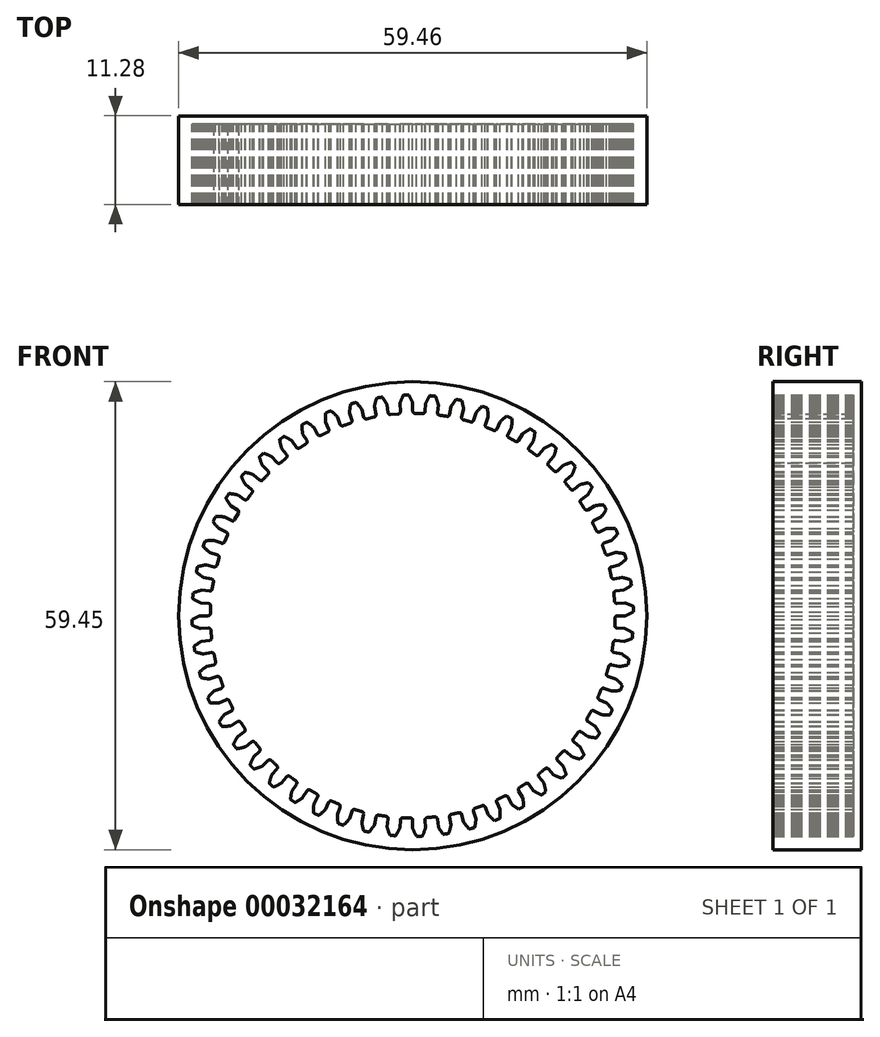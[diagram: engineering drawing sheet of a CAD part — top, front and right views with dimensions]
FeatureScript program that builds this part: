
annotation { "Feature Type Name" : "Feature", "Feature Type Description" : "" }
export const myFeature = defineFeature(function(context is Context, id is Id, definition is map)
    precondition{}
    {
        {
            var Q0;
            Q0=qCreatedBy(makeId("Front.planeOp"),FACE);
            var sketch = newSketch(context, id + "F0", { "sketchPlane" : qUnion([Q0])});
            skLineSegment(sketch, "E0", {"start": v(0, 25.05) * mm, "end": v(0, 26.31) * mm});
            skArc(sketch, "E1.trimOffspring", {"start": v(0, 26.31) * mm, "mid": v(-0.22, 26.83) * mm, "end": v(-0.48, 27.32) * mm});
            skArc(sketch, "E2.0.MirrorCS", {"start": v(-1.59, 26.26) * mm, "mid": v(-1.4, 26.8) * mm, "end": v(-1.17, 27.3) * mm});
            skLineSegment(sketch, "E3.0.MirrorCS", {"start": v(-1.51, 25) * mm, "end": v(-1.59, 26.26) * mm});
            skPoint(sketch, "E4.orphan", {"position": v(-2.02, 33.36) * mm});
            skArc(sketch, "E5.trimOffspring", {"start": v(-0.48, 27.32) * mm, "mid": v(-0.83, 27.31) * mm, "end": v(-1.17, 27.3) * mm});
            skLineSegment(sketch, "E6.1.0", {"start": v(-4.52, 24.64) * mm, "end": v(-4.75, 25.88) * mm});
            skLineSegment(sketch, "E6.1.1", {"start": v(-3.02, 24.86) * mm, "end": v(-3.18, 26.12) * mm});
            skArc(sketch, "E6.1.2", {"start": v(-4.75, 25.88) * mm, "mid": v(-4.62, 26.43) * mm, "end": v(-4.46, 26.96) * mm});
            skArc(sketch, "E6.1.3", {"start": v(-3.18, 26.12) * mm, "mid": v(-3.46, 26.6) * mm, "end": v(-3.77, 27.06) * mm});
            skArc(sketch, "E6.1.4", {"start": v(-3.77, 27.06) * mm, "mid": v(-4.12, 27.01) * mm, "end": v(-4.46, 26.96) * mm});
            skLineSegment(sketch, "E6.2.0", {"start": v(-7.46, 23.91) * mm, "end": v(-7.84, 25.12) * mm});
            skLineSegment(sketch, "E6.2.1", {"start": v(-6, 24.32) * mm, "end": v(-6.3, 25.55) * mm});
            skArc(sketch, "E6.2.2", {"start": v(-7.84, 25.12) * mm, "mid": v(-7.78, 25.68) * mm, "end": v(-7.68, 26.23) * mm});
            skArc(sketch, "E6.2.3", {"start": v(-6.3, 25.55) * mm, "mid": v(-6.64, 26) * mm, "end": v(-7.01, 26.41) * mm});
            skArc(sketch, "E6.2.4", {"start": v(-7.01, 26.41) * mm, "mid": v(-7.34, 26.32) * mm, "end": v(-7.68, 26.23) * mm});
            skLineSegment(sketch, "E6.3.0", {"start": v(-10.3, 22.84) * mm, "end": v(-10.8, 24) * mm});
            skLineSegment(sketch, "E6.3.1", {"start": v(-8.9, 23.42) * mm, "end": v(-9.34, 24.6) * mm});
            skArc(sketch, "E6.3.2", {"start": v(-10.8, 24) * mm, "mid": v(-10.82, 24.55) * mm, "end": v(-10.78, 25.1) * mm});
            skArc(sketch, "E6.3.3", {"start": v(-9.34, 24.6) * mm, "mid": v(-9.73, 25) * mm, "end": v(-10.15, 25.37) * mm});
            skArc(sketch, "E6.3.4", {"start": v(-10.15, 25.37) * mm, "mid": v(-10.47, 25.24) * mm, "end": v(-10.78, 25.1) * mm});
            skLineSegment(sketch, "E6.4.0", {"start": v(-12.97, 21.43) * mm, "end": v(-13.63, 22.51) * mm});
            skLineSegment(sketch, "E6.4.1", {"start": v(-11.65, 22.17) * mm, "end": v(-12.24, 23.3) * mm});
            skArc(sketch, "E6.4.2", {"start": v(-13.63, 22.51) * mm, "mid": v(-13.7, 23.07) * mm, "end": v(-13.74, 23.63) * mm});
            skArc(sketch, "E6.4.3", {"start": v(-12.24, 23.3) * mm, "mid": v(-12.67, 23.65) * mm, "end": v(-13.14, 23.96) * mm});
            skArc(sketch, "E6.4.4", {"start": v(-13.14, 23.96) * mm, "mid": v(-13.44, 23.8) * mm, "end": v(-13.74, 23.63) * mm});
            skLineSegment(sketch, "E6.5.0", {"start": v(-15.46, 19.71) * mm, "end": v(-16.24, 20.7) * mm});
            skLineSegment(sketch, "E6.5.1", {"start": v(-14.24, 20.6) * mm, "end": v(-14.96, 21.65) * mm});
            skArc(sketch, "E6.5.2", {"start": v(-16.24, 20.7) * mm, "mid": v(-16.39, 21.25) * mm, "end": v(-16.49, 21.8) * mm});
            skArc(sketch, "E6.5.3", {"start": v(-14.96, 21.65) * mm, "mid": v(-15.44, 21.95) * mm, "end": v(-15.93, 22.2) * mm});
            skArc(sketch, "E6.5.4", {"start": v(-15.93, 22.2) * mm, "mid": v(-16.21, 22) * mm, "end": v(-16.49, 21.8) * mm});
            skLineSegment(sketch, "E6.6.0", {"start": v(-17.73, 17.7) * mm, "end": v(-18.63, 18.6) * mm});
            skLineSegment(sketch, "E6.6.1", {"start": v(-16.63, 18.74) * mm, "end": v(-17.47, 19.69) * mm});
            skArc(sketch, "E6.6.2", {"start": v(-18.63, 18.6) * mm, "mid": v(-18.83, 19.12) * mm, "end": v(-19, 19.65) * mm});
            skArc(sketch, "E6.6.3", {"start": v(-17.47, 19.69) * mm, "mid": v(-17.97, 19.93) * mm, "end": v(-18.5, 20.12) * mm});
            skArc(sketch, "E6.6.4", {"start": v(-18.5, 20.12) * mm, "mid": v(-18.75, 19.89) * mm, "end": v(-19, 19.65) * mm});
            skLineSegment(sketch, "E6.7.0", {"start": v(-19.74, 15.44) * mm, "end": v(-20.73, 16.22) * mm});
            skLineSegment(sketch, "E6.7.1", {"start": v(-18.77, 16.6) * mm, "end": v(-19.72, 17.44) * mm});
            skArc(sketch, "E6.7.2", {"start": v(-20.73, 16.22) * mm, "mid": v(-21, 16.7) * mm, "end": v(-21.23, 17.22) * mm});
            skArc(sketch, "E6.7.3", {"start": v(-19.72, 17.44) * mm, "mid": v(-20.25, 17.62) * mm, "end": v(-20.8, 17.75) * mm});
            skArc(sketch, "E6.7.4", {"start": v(-20.8, 17.75) * mm, "mid": v(-21.01, 17.48) * mm, "end": v(-21.23, 17.22) * mm});
            skLineSegment(sketch, "E6.8.0", {"start": v(-21.46, 12.94) * mm, "end": v(-22.54, 13.6) * mm});
            skLineSegment(sketch, "E6.8.1", {"start": v(-20.64, 14.22) * mm, "end": v(-21.68, 14.93) * mm});
            skArc(sketch, "E6.8.2", {"start": v(-22.54, 13.6) * mm, "mid": v(-22.87, 14.05) * mm, "end": v(-23.16, 14.53) * mm});
            skArc(sketch, "E6.8.3", {"start": v(-21.68, 14.93) * mm, "mid": v(-22.23, 15.05) * mm, "end": v(-22.78, 15.11) * mm});
            skArc(sketch, "E6.8.4", {"start": v(-22.78, 15.11) * mm, "mid": v(-22.97, 14.82) * mm, "end": v(-23.16, 14.53) * mm});
            skLineSegment(sketch, "E6.9.0", {"start": v(-22.86, 10.26) * mm, "end": v(-24.02, 10.78) * mm});
            skLineSegment(sketch, "E6.9.1", {"start": v(-22.2, 11.62) * mm, "end": v(-23.32, 12.21) * mm});
            skArc(sketch, "E6.9.2", {"start": v(-24.02, 10.78) * mm, "mid": v(-24.4, 11.2) * mm, "end": v(-24.74, 11.64) * mm});
            skArc(sketch, "E6.9.3", {"start": v(-23.32, 12.21) * mm, "mid": v(-23.88, 12.26) * mm, "end": v(-24.44, 12.26) * mm});
            skArc(sketch, "E6.9.4", {"start": v(-24.44, 12.26) * mm, "mid": v(-24.6, 11.95) * mm, "end": v(-24.74, 11.64) * mm});
            skLineSegment(sketch, "E6.10.0", {"start": v(-23.94, 7.43) * mm, "end": v(-25.15, 7.8) * mm});
            skLineSegment(sketch, "E6.10.1", {"start": v(-23.44, 8.86) * mm, "end": v(-24.63, 9.31) * mm});
            skArc(sketch, "E6.10.2", {"start": v(-25.15, 7.8) * mm, "mid": v(-25.57, 8.17) * mm, "end": v(-25.97, 8.57) * mm});
            skArc(sketch, "E6.10.3", {"start": v(-24.63, 9.31) * mm, "mid": v(-25.19, 9.29) * mm, "end": v(-25.74, 9.22) * mm});
            skArc(sketch, "E6.10.4", {"start": v(-25.74, 9.22) * mm, "mid": v(-25.86, 8.9) * mm, "end": v(-25.97, 8.57) * mm});
            skLineSegment(sketch, "E6.11.0", {"start": v(-24.66, 4.5) * mm, "end": v(-25.9, 4.72) * mm});
            skLineSegment(sketch, "E6.11.1", {"start": v(-24.35, 5.97) * mm, "end": v(-25.58, 6.28) * mm});
            skArc(sketch, "E6.11.2", {"start": v(-25.9, 4.72) * mm, "mid": v(-26.38, 5.03) * mm, "end": v(-26.81, 5.38) * mm});
            skArc(sketch, "E6.11.3", {"start": v(-25.58, 6.28) * mm, "mid": v(-26.13, 6.18) * mm, "end": v(-26.67, 6.05) * mm});
            skArc(sketch, "E6.11.4", {"start": v(-26.67, 6.05) * mm, "mid": v(-26.74, 5.71) * mm, "end": v(-26.81, 5.38) * mm});
            skLineSegment(sketch, "E6.12.0", {"start": v(-25.03, 1.49) * mm, "end": v(-26.3, 1.56) * mm});
            skLineSegment(sketch, "E6.12.1", {"start": v(-24.9, 3) * mm, "end": v(-26.15, 3.15) * mm});
            skArc(sketch, "E6.12.2", {"start": v(-26.3, 1.56) * mm, "mid": v(-26.8, 1.81) * mm, "end": v(-27.27, 2.1) * mm});
            skArc(sketch, "E6.12.3", {"start": v(-26.15, 3.15) * mm, "mid": v(-26.69, 3) * mm, "end": v(-27.2, 2.8) * mm});
            skArc(sketch, "E6.12.4", {"start": v(-27.2, 2.8) * mm, "mid": v(-27.24, 2.45) * mm, "end": v(-27.27, 2.1) * mm});
            skLineSegment(sketch, "E6.13.0", {"start": v(-25.03, -1.54) * mm, "end": v(-26.3, -1.62) * mm});
            skLineSegment(sketch, "E6.13.1", {"start": v(-25.07, -0.03) * mm, "end": v(-26.34, -0.03) * mm});
            skArc(sketch, "E6.13.2", {"start": v(-26.3, -1.62) * mm, "mid": v(-26.82, -1.43) * mm, "end": v(-27.33, -1.2) * mm});
            skArc(sketch, "E6.13.3", {"start": v(-26.34, -0.03) * mm, "mid": v(-26.85, -0.25) * mm, "end": v(-27.35, -0.5) * mm});
            skArc(sketch, "E6.13.4", {"start": v(-27.35, -0.5) * mm, "mid": v(-27.34, -0.85) * mm, "end": v(-27.33, -1.2) * mm});
            skLineSegment(sketch, "E6.14.0", {"start": v(-24.66, -4.55) * mm, "end": v(-25.9, -4.78) * mm});
            skLineSegment(sketch, "E6.14.1", {"start": v(-24.9, -3.05) * mm, "end": v(-26.15, -3.2) * mm});
            skArc(sketch, "E6.14.2", {"start": v(-25.9, -4.78) * mm, "mid": v(-26.45, -4.65) * mm, "end": v(-26.99, -4.48) * mm});
            skArc(sketch, "E6.14.3", {"start": v(-26.15, -3.2) * mm, "mid": v(-26.63, -3.48) * mm, "end": v(-27.1, -3.8) * mm});
            skArc(sketch, "E6.14.4", {"start": v(-27.1, -3.8) * mm, "mid": v(-27.04, -4.14) * mm, "end": v(-26.99, -4.48) * mm});
            skLineSegment(sketch, "E6.15.0", {"start": v(-23.94, -7.49) * mm, "end": v(-25.15, -7.86) * mm});
            skLineSegment(sketch, "E6.15.1", {"start": v(-24.35, -6.03) * mm, "end": v(-25.58, -6.33) * mm});
            skArc(sketch, "E6.15.2", {"start": v(-25.15, -7.86) * mm, "mid": v(-25.7, -7.8) * mm, "end": v(-26.25, -7.7) * mm});
            skArc(sketch, "E6.15.3", {"start": v(-25.58, -6.33) * mm, "mid": v(-26.02, -6.67) * mm, "end": v(-26.44, -7.04) * mm});
            skArc(sketch, "E6.15.4", {"start": v(-26.44, -7.04) * mm, "mid": v(-26.35, -7.37) * mm, "end": v(-26.25, -7.7) * mm});
            skLineSegment(sketch, "E6.16.0", {"start": v(-22.87, -10.32) * mm, "end": v(-24.02, -10.84) * mm});
            skLineSegment(sketch, "E6.16.1", {"start": v(-23.44, -8.92) * mm, "end": v(-24.63, -9.37) * mm});
            skArc(sketch, "E6.16.2", {"start": v(-24.02, -10.84) * mm, "mid": v(-24.58, -10.85) * mm, "end": v(-25.14, -10.81) * mm});
            skArc(sketch, "E6.16.3", {"start": v(-24.63, -9.37) * mm, "mid": v(-25.03, -9.76) * mm, "end": v(-25.4, -10.18) * mm});
            skArc(sketch, "E6.16.4", {"start": v(-25.4, -10.18) * mm, "mid": v(-25.27, -10.5) * mm, "end": v(-25.14, -10.81) * mm});
            skLineSegment(sketch, "E6.17.0", {"start": v(-21.46, -13) * mm, "end": v(-22.54, -13.65) * mm});
            skLineSegment(sketch, "E6.17.1", {"start": v(-22.2, -11.68) * mm, "end": v(-23.32, -12.27) * mm});
            skArc(sketch, "E6.17.2", {"start": v(-22.54, -13.65) * mm, "mid": v(-23.1, -13.73) * mm, "end": v(-23.65, -13.76) * mm});
            skArc(sketch, "E6.17.3", {"start": v(-23.32, -12.27) * mm, "mid": v(-23.68, -12.7) * mm, "end": v(-24, -13.16) * mm});
            skArc(sketch, "E6.17.4", {"start": v(-24, -13.16) * mm, "mid": v(-23.83, -13.47) * mm, "end": v(-23.65, -13.76) * mm});
            skLineSegment(sketch, "E6.18.0", {"start": v(-19.74, -15.5) * mm, "end": v(-20.74, -16.27) * mm});
            skLineSegment(sketch, "E6.18.1", {"start": v(-20.64, -14.27) * mm, "end": v(-21.68, -15) * mm});
            skArc(sketch, "E6.18.2", {"start": v(-20.74, -16.27) * mm, "mid": v(-21.28, -16.42) * mm, "end": v(-21.83, -16.52) * mm});
            skArc(sketch, "E6.18.3", {"start": v(-21.68, -15) * mm, "mid": v(-21.98, -15.46) * mm, "end": v(-22.23, -15.96) * mm});
            skArc(sketch, "E6.18.4", {"start": v(-22.23, -15.96) * mm, "mid": v(-22.03, -16.24) * mm, "end": v(-21.83, -16.52) * mm});
            skLineSegment(sketch, "E6.19.0", {"start": v(-17.73, -17.76) * mm, "end": v(-18.63, -18.65) * mm});
            skLineSegment(sketch, "E6.19.1", {"start": v(-18.77, -16.66) * mm, "end": v(-19.72, -17.5) * mm});
            skArc(sketch, "E6.19.2", {"start": v(-18.63, -18.65) * mm, "mid": v(-19.15, -18.86) * mm, "end": v(-19.68, -19.03) * mm});
            skArc(sketch, "E6.19.3", {"start": v(-19.72, -17.5) * mm, "mid": v(-19.96, -18) * mm, "end": v(-20.15, -18.52) * mm});
            skArc(sketch, "E6.19.4", {"start": v(-20.15, -18.52) * mm, "mid": v(-19.92, -18.78) * mm, "end": v(-19.68, -19.03) * mm});
            skLineSegment(sketch, "E6.20.0", {"start": v(-15.46, -19.77) * mm, "end": v(-16.25, -20.76) * mm});
            skLineSegment(sketch, "E6.20.1", {"start": v(-16.63, -18.8) * mm, "end": v(-17.47, -19.74) * mm});
            skArc(sketch, "E6.20.2", {"start": v(-16.25, -20.76) * mm, "mid": v(-16.74, -21.03) * mm, "end": v(-17.25, -21.26) * mm});
            skArc(sketch, "E6.20.3", {"start": v(-17.47, -19.74) * mm, "mid": v(-17.64, -20.28) * mm, "end": v(-17.78, -20.82) * mm});
            skArc(sketch, "E6.20.4", {"start": v(-17.78, -20.82) * mm, "mid": v(-17.51, -21.04) * mm, "end": v(-17.25, -21.26) * mm});
            skLineSegment(sketch, "E6.21.0", {"start": v(-12.97, -21.49) * mm, "end": v(-13.63, -22.57) * mm});
            skLineSegment(sketch, "E6.21.1", {"start": v(-14.24, -20.66) * mm, "end": v(-14.96, -21.7) * mm});
            skArc(sketch, "E6.21.2", {"start": v(-13.63, -22.57) * mm, "mid": v(-14.08, -22.9) * mm, "end": v(-14.56, -23.18) * mm});
            skArc(sketch, "E6.21.3", {"start": v(-14.96, -21.7) * mm, "mid": v(-15.07, -22.25) * mm, "end": v(-15.14, -22.8) * mm});
            skArc(sketch, "E6.21.4", {"start": v(-15.14, -22.8) * mm, "mid": v(-14.85, -23) * mm, "end": v(-14.56, -23.18) * mm});
            skLineSegment(sketch, "E6.22.0", {"start": v(-10.3, -22.9) * mm, "end": v(-10.81, -24.05) * mm});
            skLineSegment(sketch, "E6.22.1", {"start": v(-11.65, -22.23) * mm, "end": v(-12.24, -23.35) * mm});
            skArc(sketch, "E6.22.2", {"start": v(-10.81, -24.05) * mm, "mid": v(-11.22, -24.43) * mm, "end": v(-11.66, -24.77) * mm});
            skArc(sketch, "E6.22.3", {"start": v(-12.24, -23.35) * mm, "mid": v(-12.29, -23.9) * mm, "end": v(-12.28, -24.47) * mm});
            skArc(sketch, "E6.22.4", {"start": v(-12.28, -24.47) * mm, "mid": v(-11.97, -24.62) * mm, "end": v(-11.66, -24.77) * mm});
            skLineSegment(sketch, "E6.23.0", {"start": v(-7.46, -23.97) * mm, "end": v(-7.84, -25.18) * mm});
            skLineSegment(sketch, "E6.23.1", {"start": v(-8.9, -23.47) * mm, "end": v(-9.34, -24.66) * mm});
            skArc(sketch, "E6.23.2", {"start": v(-7.84, -25.18) * mm, "mid": v(-8.2, -25.6) * mm, "end": v(-8.6, -26) * mm});
            skArc(sketch, "E6.23.3", {"start": v(-9.34, -24.66) * mm, "mid": v(-9.32, -25.22) * mm, "end": v(-9.25, -25.77) * mm});
            skArc(sketch, "E6.23.4", {"start": v(-9.25, -25.77) * mm, "mid": v(-8.92, -25.89) * mm, "end": v(-8.6, -26) * mm});
            skLineSegment(sketch, "E6.24.0", {"start": v(-4.52, -24.7) * mm, "end": v(-4.75, -25.94) * mm});
            skLineSegment(sketch, "E6.24.1", {"start": v(-6, -24.37) * mm, "end": v(-6.3, -25.6) * mm});
            skArc(sketch, "E6.24.2", {"start": v(-4.75, -25.94) * mm, "mid": v(-5.06, -26.4) * mm, "end": v(-5.4, -26.84) * mm});
            skArc(sketch, "E6.24.3", {"start": v(-6.3, -25.6) * mm, "mid": v(-6.21, -26.16) * mm, "end": v(-6.08, -26.7) * mm});
            skArc(sketch, "E6.24.4", {"start": v(-6.08, -26.7) * mm, "mid": v(-5.74, -26.77) * mm, "end": v(-5.4, -26.84) * mm});
            skLineSegment(sketch, "E6.25.0", {"start": v(-1.51, -25.06) * mm, "end": v(-1.6, -26.32) * mm});
            skLineSegment(sketch, "E6.25.1", {"start": v(-3.02, -24.92) * mm, "end": v(-3.18, -26.18) * mm});
            skArc(sketch, "E6.25.2", {"start": v(-1.6, -26.32) * mm, "mid": v(-1.84, -26.82) * mm, "end": v(-2.13, -27.3) * mm});
            skArc(sketch, "E6.25.3", {"start": v(-3.18, -26.18) * mm, "mid": v(-3.02, -26.71) * mm, "end": v(-2.82, -27.24) * mm});
            skArc(sketch, "E6.25.4", {"start": v(-2.82, -27.24) * mm, "mid": v(-2.48, -27.27) * mm, "end": v(-2.13, -27.3) * mm});
            skLineSegment(sketch, "E6.26.0", {"start": v(1.51, -25.06) * mm, "end": v(1.59, -26.32) * mm});
            skLineSegment(sketch, "E6.26.1", {"start": v(0, -25.1) * mm, "end": v(0, -26.37) * mm});
            skArc(sketch, "E6.26.2", {"start": v(1.59, -26.32) * mm, "mid": v(1.4, -26.85) * mm, "end": v(1.17, -27.36) * mm});
            skArc(sketch, "E6.26.3", {"start": v(0, -26.37) * mm, "mid": v(0.22, -26.88) * mm, "end": v(0.48, -27.38) * mm});
            skArc(sketch, "E6.26.4", {"start": v(0.48, -27.38) * mm, "mid": v(0.83, -27.37) * mm, "end": v(1.17, -27.36) * mm});
            skLineSegment(sketch, "E6.27.0", {"start": v(4.52, -24.7) * mm, "end": v(4.75, -25.94) * mm});
            skLineSegment(sketch, "E6.27.1", {"start": v(3.02, -24.92) * mm, "end": v(3.18, -26.18) * mm});
            skArc(sketch, "E6.27.2", {"start": v(4.75, -25.94) * mm, "mid": v(4.62, -26.48) * mm, "end": v(4.46, -27.02) * mm});
            skArc(sketch, "E6.27.3", {"start": v(3.18, -26.18) * mm, "mid": v(3.46, -26.66) * mm, "end": v(3.77, -27.12) * mm});
            skArc(sketch, "E6.27.4", {"start": v(3.77, -27.12) * mm, "mid": v(4.12, -27.07) * mm, "end": v(4.46, -27.02) * mm});
            skLineSegment(sketch, "E6.28.0", {"start": v(7.46, -23.97) * mm, "end": v(7.84, -25.18) * mm});
            skLineSegment(sketch, "E6.28.1", {"start": v(6, -24.37) * mm, "end": v(6.3, -25.6) * mm});
            skArc(sketch, "E6.28.2", {"start": v(7.84, -25.18) * mm, "mid": v(7.78, -25.73) * mm, "end": v(7.68, -26.28) * mm});
            skArc(sketch, "E6.28.3", {"start": v(6.3, -25.6) * mm, "mid": v(6.64, -26.05) * mm, "end": v(7.01, -26.47) * mm});
            skArc(sketch, "E6.28.4", {"start": v(7.01, -26.47) * mm, "mid": v(7.34, -26.38) * mm, "end": v(7.68, -26.28) * mm});
            skLineSegment(sketch, "E6.29.0", {"start": v(10.3, -22.9) * mm, "end": v(10.8, -24.05) * mm});
            skLineSegment(sketch, "E6.29.1", {"start": v(8.9, -23.47) * mm, "end": v(9.34, -24.66) * mm});
            skArc(sketch, "E6.29.2", {"start": v(10.8, -24.05) * mm, "mid": v(10.82, -24.6) * mm, "end": v(10.78, -25.17) * mm});
            skArc(sketch, "E6.29.3", {"start": v(9.34, -24.66) * mm, "mid": v(9.73, -25.06) * mm, "end": v(10.15, -25.43) * mm});
            skArc(sketch, "E6.29.4", {"start": v(10.15, -25.43) * mm, "mid": v(10.47, -25.3) * mm, "end": v(10.78, -25.17) * mm});
            skLineSegment(sketch, "E6.30.0", {"start": v(12.97, -21.49) * mm, "end": v(13.63, -22.57) * mm});
            skLineSegment(sketch, "E6.30.1", {"start": v(11.65, -22.23) * mm, "end": v(12.24, -23.35) * mm});
            skArc(sketch, "E6.30.2", {"start": v(13.63, -22.57) * mm, "mid": v(13.7, -23.12) * mm, "end": v(13.74, -23.68) * mm});
            skArc(sketch, "E6.30.3", {"start": v(12.24, -23.35) * mm, "mid": v(12.67, -23.7) * mm, "end": v(13.14, -24.02) * mm});
            skArc(sketch, "E6.30.4", {"start": v(13.14, -24.02) * mm, "mid": v(13.44, -23.85) * mm, "end": v(13.74, -23.68) * mm});
            skLineSegment(sketch, "E6.31.0", {"start": v(15.46, -19.77) * mm, "end": v(16.24, -20.76) * mm});
            skLineSegment(sketch, "E6.31.1", {"start": v(14.24, -20.66) * mm, "end": v(14.96, -21.7) * mm});
            skArc(sketch, "E6.31.2", {"start": v(16.24, -20.76) * mm, "mid": v(16.39, -21.3) * mm, "end": v(16.49, -21.85) * mm});
            skArc(sketch, "E6.31.3", {"start": v(14.96, -21.7) * mm, "mid": v(15.44, -22) * mm, "end": v(15.93, -22.26) * mm});
            skArc(sketch, "E6.31.4", {"start": v(15.93, -22.26) * mm, "mid": v(16.21, -22.06) * mm, "end": v(16.49, -21.85) * mm});
            skLineSegment(sketch, "E6.32.0", {"start": v(17.73, -17.76) * mm, "end": v(18.63, -18.65) * mm});
            skLineSegment(sketch, "E6.32.1", {"start": v(16.63, -18.8) * mm, "end": v(17.47, -19.74) * mm});
            skArc(sketch, "E6.32.2", {"start": v(18.63, -18.65) * mm, "mid": v(18.83, -19.17) * mm, "end": v(19, -19.7) * mm});
            skArc(sketch, "E6.32.3", {"start": v(17.47, -19.74) * mm, "mid": v(17.97, -19.98) * mm, "end": v(18.5, -20.18) * mm});
            skArc(sketch, "E6.32.4", {"start": v(18.5, -20.18) * mm, "mid": v(18.75, -19.95) * mm, "end": v(19, -19.7) * mm});
            skLineSegment(sketch, "E6.33.0", {"start": v(19.74, -15.5) * mm, "end": v(20.73, -16.27) * mm});
            skLineSegment(sketch, "E6.33.1", {"start": v(18.77, -16.66) * mm, "end": v(19.72, -17.5) * mm});
            skArc(sketch, "E6.33.2", {"start": v(20.73, -16.27) * mm, "mid": v(21, -16.76) * mm, "end": v(21.23, -17.27) * mm});
            skArc(sketch, "E6.33.3", {"start": v(19.72, -17.5) * mm, "mid": v(20.25, -17.67) * mm, "end": v(20.8, -17.8) * mm});
            skArc(sketch, "E6.33.4", {"start": v(20.8, -17.8) * mm, "mid": v(21.01, -17.54) * mm, "end": v(21.23, -17.27) * mm});
            skLineSegment(sketch, "E6.34.0", {"start": v(21.46, -13) * mm, "end": v(22.54, -13.66) * mm});
            skLineSegment(sketch, "E6.34.1", {"start": v(20.64, -14.27) * mm, "end": v(21.68, -15) * mm});
            skArc(sketch, "E6.34.2", {"start": v(22.54, -13.66) * mm, "mid": v(22.87, -14.11) * mm, "end": v(23.16, -14.59) * mm});
            skArc(sketch, "E6.34.3", {"start": v(21.68, -15) * mm, "mid": v(22.23, -15.1) * mm, "end": v(22.78, -15.17) * mm});
            skArc(sketch, "E6.34.4", {"start": v(22.78, -15.17) * mm, "mid": v(22.97, -14.88) * mm, "end": v(23.16, -14.59) * mm});
            skLineSegment(sketch, "E6.35.0", {"start": v(22.86, -10.32) * mm, "end": v(24.02, -10.84) * mm});
            skLineSegment(sketch, "E6.35.1", {"start": v(22.2, -11.68) * mm, "end": v(23.32, -12.27) * mm});
            skArc(sketch, "E6.35.2", {"start": v(24.02, -10.84) * mm, "mid": v(24.4, -11.25) * mm, "end": v(24.74, -11.7) * mm});
            skArc(sketch, "E6.35.3", {"start": v(23.32, -12.27) * mm, "mid": v(23.88, -12.31) * mm, "end": v(24.44, -12.31) * mm});
            skArc(sketch, "E6.35.4", {"start": v(24.44, -12.31) * mm, "mid": v(24.6, -12) * mm, "end": v(24.74, -11.7) * mm});
            skLineSegment(sketch, "E6.36.0", {"start": v(23.94, -7.49) * mm, "end": v(25.15, -7.87) * mm});
            skLineSegment(sketch, "E6.36.1", {"start": v(23.44, -8.92) * mm, "end": v(24.63, -9.37) * mm});
            skArc(sketch, "E6.36.2", {"start": v(25.15, -7.87) * mm, "mid": v(25.57, -8.23) * mm, "end": v(25.97, -8.63) * mm});
            skArc(sketch, "E6.36.3", {"start": v(24.63, -9.37) * mm, "mid": v(25.19, -9.35) * mm, "end": v(25.74, -9.28) * mm});
            skArc(sketch, "E6.36.4", {"start": v(25.74, -9.28) * mm, "mid": v(25.86, -8.95) * mm, "end": v(25.97, -8.63) * mm});
            skLineSegment(sketch, "E6.37.0", {"start": v(24.66, -4.55) * mm, "end": v(25.9, -4.78) * mm});
            skLineSegment(sketch, "E6.37.1", {"start": v(24.35, -6.03) * mm, "end": v(25.58, -6.33) * mm});
            skArc(sketch, "E6.37.2", {"start": v(25.9, -4.78) * mm, "mid": v(26.38, -5.09) * mm, "end": v(26.81, -5.43) * mm});
            skArc(sketch, "E6.37.3", {"start": v(25.58, -6.33) * mm, "mid": v(26.13, -6.24) * mm, "end": v(26.67, -6.1) * mm});
            skArc(sketch, "E6.37.4", {"start": v(26.67, -6.1) * mm, "mid": v(26.74, -5.77) * mm, "end": v(26.81, -5.43) * mm});
            skLineSegment(sketch, "E6.38.0", {"start": v(25.03, -1.54) * mm, "end": v(26.3, -1.62) * mm});
            skLineSegment(sketch, "E6.38.1", {"start": v(24.9, -3.05) * mm, "end": v(26.15, -3.2) * mm});
            skArc(sketch, "E6.38.2", {"start": v(26.3, -1.62) * mm, "mid": v(26.8, -1.87) * mm, "end": v(27.27, -2.16) * mm});
            skArc(sketch, "E6.38.3", {"start": v(26.15, -3.2) * mm, "mid": v(26.69, -3.05) * mm, "end": v(27.2, -2.85) * mm});
            skArc(sketch, "E6.38.4", {"start": v(27.2, -2.85) * mm, "mid": v(27.24, -2.5) * mm, "end": v(27.27, -2.16) * mm});
            skLineSegment(sketch, "E6.39.0", {"start": v(25.03, 1.48) * mm, "end": v(26.3, 1.56) * mm});
            skLineSegment(sketch, "E6.39.1", {"start": v(25.07, -0.03) * mm, "end": v(26.34, -0.03) * mm});
            skArc(sketch, "E6.39.2", {"start": v(26.3, 1.56) * mm, "mid": v(26.82, 1.37) * mm, "end": v(27.33, 1.14) * mm});
            skArc(sketch, "E6.39.3", {"start": v(26.34, -0.03) * mm, "mid": v(26.85, 0.2) * mm, "end": v(27.35, 0.45) * mm});
            skArc(sketch, "E6.39.4", {"start": v(27.35, 0.45) * mm, "mid": v(27.34, 0.8) * mm, "end": v(27.33, 1.14) * mm});
            skLineSegment(sketch, "E6.40.0", {"start": v(24.66, 4.5) * mm, "end": v(25.9, 4.72) * mm});
            skLineSegment(sketch, "E6.40.1", {"start": v(24.9, 3) * mm, "end": v(26.15, 3.15) * mm});
            skArc(sketch, "E6.40.2", {"start": v(25.9, 4.72) * mm, "mid": v(26.45, 4.6) * mm, "end": v(26.99, 4.43) * mm});
            skArc(sketch, "E6.40.3", {"start": v(26.15, 3.15) * mm, "mid": v(26.63, 3.43) * mm, "end": v(27.1, 3.75) * mm});
            skArc(sketch, "E6.40.4", {"start": v(27.1, 3.75) * mm, "mid": v(27.04, 4.09) * mm, "end": v(26.99, 4.43) * mm});
            skLineSegment(sketch, "E6.41.0", {"start": v(23.94, 7.43) * mm, "end": v(25.15, 7.8) * mm});
            skLineSegment(sketch, "E6.41.1", {"start": v(24.35, 5.97) * mm, "end": v(25.58, 6.28) * mm});
            skArc(sketch, "E6.41.2", {"start": v(25.15, 7.8) * mm, "mid": v(25.7, 7.75) * mm, "end": v(26.25, 7.65) * mm});
            skArc(sketch, "E6.41.3", {"start": v(25.58, 6.28) * mm, "mid": v(26.02, 6.61) * mm, "end": v(26.44, 6.98) * mm});
            skArc(sketch, "E6.41.4", {"start": v(26.44, 6.98) * mm, "mid": v(26.35, 7.32) * mm, "end": v(26.25, 7.65) * mm});
            skLineSegment(sketch, "E6.42.0", {"start": v(22.87, 10.26) * mm, "end": v(24.02, 10.78) * mm});
            skLineSegment(sketch, "E6.42.1", {"start": v(23.44, 8.86) * mm, "end": v(24.63, 9.31) * mm});
            skArc(sketch, "E6.42.2", {"start": v(24.02, 10.78) * mm, "mid": v(24.58, 10.8) * mm, "end": v(25.14, 10.76) * mm});
            skArc(sketch, "E6.42.3", {"start": v(24.63, 9.31) * mm, "mid": v(25.03, 9.7) * mm, "end": v(25.4, 10.12) * mm});
            skArc(sketch, "E6.42.4", {"start": v(25.4, 10.12) * mm, "mid": v(25.27, 10.44) * mm, "end": v(25.14, 10.76) * mm});
            skLineSegment(sketch, "E6.43.0", {"start": v(21.46, 12.94) * mm, "end": v(22.54, 13.6) * mm});
            skLineSegment(sketch, "E6.43.1", {"start": v(22.2, 11.62) * mm, "end": v(23.32, 12.21) * mm});
            skArc(sketch, "E6.43.2", {"start": v(22.54, 13.6) * mm, "mid": v(23.1, 13.68) * mm, "end": v(23.65, 13.7) * mm});
            skArc(sketch, "E6.43.3", {"start": v(23.32, 12.21) * mm, "mid": v(23.68, 12.65) * mm, "end": v(24, 13.1) * mm});
            skArc(sketch, "E6.43.4", {"start": v(24, 13.1) * mm, "mid": v(23.83, 13.4) * mm, "end": v(23.65, 13.7) * mm});
            skLineSegment(sketch, "E6.44.0", {"start": v(19.74, 15.43) * mm, "end": v(20.74, 16.22) * mm});
            skLineSegment(sketch, "E6.44.1", {"start": v(20.64, 14.22) * mm, "end": v(21.68, 14.93) * mm});
            skArc(sketch, "E6.44.2", {"start": v(20.74, 16.22) * mm, "mid": v(21.28, 16.36) * mm, "end": v(21.83, 16.46) * mm});
            skArc(sketch, "E6.44.3", {"start": v(21.68, 14.93) * mm, "mid": v(21.98, 15.4) * mm, "end": v(22.23, 15.9) * mm});
            skArc(sketch, "E6.44.4", {"start": v(22.23, 15.9) * mm, "mid": v(22.03, 16.18) * mm, "end": v(21.83, 16.46) * mm});
            skLineSegment(sketch, "E6.45.0", {"start": v(17.73, 17.7) * mm, "end": v(18.63, 18.6) * mm});
            skLineSegment(sketch, "E6.45.1", {"start": v(18.77, 16.6) * mm, "end": v(19.72, 17.44) * mm});
            skArc(sketch, "E6.45.2", {"start": v(18.63, 18.6) * mm, "mid": v(19.15, 18.8) * mm, "end": v(19.68, 18.97) * mm});
            skArc(sketch, "E6.45.3", {"start": v(19.72, 17.44) * mm, "mid": v(19.96, 17.94) * mm, "end": v(20.15, 18.47) * mm});
            skArc(sketch, "E6.45.4", {"start": v(20.15, 18.47) * mm, "mid": v(19.92, 18.72) * mm, "end": v(19.68, 18.97) * mm});
            skLineSegment(sketch, "E6.46.0", {"start": v(15.46, 19.7) * mm, "end": v(16.25, 20.7) * mm});
            skLineSegment(sketch, "E6.46.1", {"start": v(16.63, 18.74) * mm, "end": v(17.47, 19.69) * mm});
            skArc(sketch, "E6.46.2", {"start": v(16.25, 20.7) * mm, "mid": v(16.74, 20.98) * mm, "end": v(17.25, 21.2) * mm});
            skArc(sketch, "E6.46.3", {"start": v(17.47, 19.69) * mm, "mid": v(17.64, 20.22) * mm, "end": v(17.78, 20.76) * mm});
            skArc(sketch, "E6.46.4", {"start": v(17.78, 20.76) * mm, "mid": v(17.51, 20.98) * mm, "end": v(17.25, 21.2) * mm});
            skLineSegment(sketch, "E6.47.0", {"start": v(12.97, 21.43) * mm, "end": v(13.63, 22.51) * mm});
            skLineSegment(sketch, "E6.47.1", {"start": v(14.24, 20.6) * mm, "end": v(14.96, 21.65) * mm});
            skArc(sketch, "E6.47.2", {"start": v(13.63, 22.51) * mm, "mid": v(14.08, 22.84) * mm, "end": v(14.56, 23.13) * mm});
            skArc(sketch, "E6.47.3", {"start": v(14.96, 21.65) * mm, "mid": v(15.07, 22.2) * mm, "end": v(15.14, 22.75) * mm});
            skArc(sketch, "E6.47.4", {"start": v(15.14, 22.75) * mm, "mid": v(14.85, 22.94) * mm, "end": v(14.56, 23.13) * mm});
            skLineSegment(sketch, "E6.48.0", {"start": v(10.3, 22.84) * mm, "end": v(10.81, 24) * mm});
            skLineSegment(sketch, "E6.48.1", {"start": v(11.65, 22.17) * mm, "end": v(12.24, 23.3) * mm});
            skArc(sketch, "E6.48.2", {"start": v(10.81, 24) * mm, "mid": v(11.22, 24.37) * mm, "end": v(11.66, 24.71) * mm});
            skArc(sketch, "E6.48.3", {"start": v(12.24, 23.3) * mm, "mid": v(12.29, 23.85) * mm, "end": v(12.28, 24.41) * mm});
            skArc(sketch, "E6.48.4", {"start": v(12.28, 24.41) * mm, "mid": v(11.97, 24.56) * mm, "end": v(11.66, 24.71) * mm});
            skLineSegment(sketch, "E6.49.0", {"start": v(7.46, 23.91) * mm, "end": v(7.84, 25.12) * mm});
            skLineSegment(sketch, "E6.49.1", {"start": v(8.9, 23.42) * mm, "end": v(9.34, 24.6) * mm});
            skArc(sketch, "E6.49.2", {"start": v(7.84, 25.12) * mm, "mid": v(8.2, 25.54) * mm, "end": v(8.6, 25.94) * mm});
            skArc(sketch, "E6.49.3", {"start": v(9.34, 24.6) * mm, "mid": v(9.32, 25.16) * mm, "end": v(9.25, 25.71) * mm});
            skArc(sketch, "E6.49.4", {"start": v(9.25, 25.71) * mm, "mid": v(8.92, 25.83) * mm, "end": v(8.6, 25.94) * mm});
            skLineSegment(sketch, "E6.50.0", {"start": v(4.52, 24.64) * mm, "end": v(4.75, 25.88) * mm});
            skLineSegment(sketch, "E6.50.1", {"start": v(6, 24.32) * mm, "end": v(6.3, 25.55) * mm});
            skArc(sketch, "E6.50.2", {"start": v(4.75, 25.88) * mm, "mid": v(5.06, 26.35) * mm, "end": v(5.4, 26.79) * mm});
            skArc(sketch, "E6.50.3", {"start": v(6.3, 25.55) * mm, "mid": v(6.21, 26.1) * mm, "end": v(6.08, 26.64) * mm});
            skArc(sketch, "E6.50.4", {"start": v(6.08, 26.64) * mm, "mid": v(5.74, 26.72) * mm, "end": v(5.4, 26.79) * mm});
            skLineSegment(sketch, "E6.51.0", {"start": v(1.51, 25) * mm, "end": v(1.6, 26.26) * mm});
            skLineSegment(sketch, "E6.51.1", {"start": v(3.02, 24.86) * mm, "end": v(3.18, 26.12) * mm});
            skArc(sketch, "E6.51.2", {"start": v(1.6, 26.26) * mm, "mid": v(1.84, 26.76) * mm, "end": v(2.13, 27.24) * mm});
            skArc(sketch, "E6.51.3", {"start": v(3.18, 26.12) * mm, "mid": v(3.02, 26.66) * mm, "end": v(2.82, 27.18) * mm});
            skArc(sketch, "E6.51.4", {"start": v(2.82, 27.18) * mm, "mid": v(2.48, 27.21) * mm, "end": v(2.13, 27.24) * mm});
            skCircle(sketch, "E7", {"center": v(0, -0.03) * mm, "radius": 29 * mm});
            skArc(sketch, "E8.trimOffspring", {"start": v(1.51, 25) * mm, "mid": v(0.76, 25.03) * mm, "end": v(0, 25.05) * mm});
            skArc(sketch, "E9.trimOffspring", {"start": v(4.52, 24.64) * mm, "mid": v(3.77, 24.76) * mm, "end": v(3.02, 24.86) * mm});
            skArc(sketch, "E10.trimOffspring", {"start": v(7.46, 23.91) * mm, "mid": v(6.73, 24.12) * mm, "end": v(6, 24.32) * mm});
            skArc(sketch, "E11.trimOffspring", {"start": v(10.3, 22.84) * mm, "mid": v(9.6, 23.14) * mm, "end": v(8.9, 23.42) * mm});
            skArc(sketch, "E12.trimOffspring", {"start": v(12.97, 21.43) * mm, "mid": v(12.32, 21.81) * mm, "end": v(11.65, 22.17) * mm});
            skArc(sketch, "E13.trimOffspring", {"start": v(15.46, 19.7) * mm, "mid": v(14.86, 20.17) * mm, "end": v(14.24, 20.6) * mm});
            skArc(sketch, "E14.trimOffspring", {"start": v(17.73, 17.7) * mm, "mid": v(17.19, 18.23) * mm, "end": v(16.63, 18.74) * mm});
            skArc(sketch, "E15.trimOffspring", {"start": v(19.74, 15.43) * mm, "mid": v(19.26, 16.02) * mm, "end": v(18.77, 16.6) * mm});
            skArc(sketch, "E16.trimOffspring", {"start": v(21.46, 12.94) * mm, "mid": v(21.06, 13.59) * mm, "end": v(20.64, 14.22) * mm});
            skArc(sketch, "E17.trimOffspring", {"start": v(22.87, 10.26) * mm, "mid": v(22.54, 10.95) * mm, "end": v(22.2, 11.62) * mm});
            skArc(sketch, "E18.trimOffspring", {"start": v(23.94, 7.43) * mm, "mid": v(23.7, 8.15) * mm, "end": v(23.44, 8.86) * mm});
            skArc(sketch, "E19.trimOffspring", {"start": v(-7.46, 23.91) * mm, "mid": v(-8.18, 23.67) * mm, "end": v(-8.9, 23.42) * mm});
            skArc(sketch, "E20.trimOffspring", {"start": v(-12.97, 21.43) * mm, "mid": v(-13.61, 21.03) * mm, "end": v(-14.24, 20.6) * mm});
            skLineSegment(sketch, "E21", {"start": v(-6, 24.32) * mm, "end": v(-4.52, 24.64) * mm});
            skLineSegment(sketch, "E22", {"start": v(-3.02, 24.86) * mm, "end": v(-1.51, 25) * mm});
            skArc(sketch, "E23.trimOffspring", {"start": v(-10.3, 22.84) * mm, "mid": v(-10.98, 22.52) * mm, "end": v(-11.65, 22.17) * mm});
            skArc(sketch, "E24.trimOffspring", {"start": v(-17.73, 17.7) * mm, "mid": v(-18.26, 17.16) * mm, "end": v(-18.77, 16.6) * mm});
            skArc(sketch, "E25.trimOffspring", {"start": v(-19.74, 15.44) * mm, "mid": v(-20.2, 14.83) * mm, "end": v(-20.64, 14.22) * mm});
            skArc(sketch, "E26.trimOffspring", {"start": v(-25.03, 1.49) * mm, "mid": v(-25.06, 0.73) * mm, "end": v(-25.07, -0.03) * mm});
            skArc(sketch, "E27.trimOffspring", {"start": v(-25.03, -1.54) * mm, "mid": v(-24.97, -2.3) * mm, "end": v(-24.9, -3.05) * mm});
            skArc(sketch, "E28.trimOffspring", {"start": v(-24.66, -4.55) * mm, "mid": v(-24.52, -5.3) * mm, "end": v(-24.35, -6.03) * mm});
            skArc(sketch, "E29.trimOffspring", {"start": v(-23.94, -7.49) * mm, "mid": v(-23.7, -8.2) * mm, "end": v(-23.44, -8.92) * mm});
            skArc(sketch, "E30.trimOffspring", {"start": v(24.66, 4.5) * mm, "mid": v(24.52, 5.23) * mm, "end": v(24.35, 5.97) * mm});
            skArc(sketch, "E31.trimOffspring", {"start": v(25.03, 1.48) * mm, "mid": v(24.97, 2.24) * mm, "end": v(24.9, 3) * mm});
            skArc(sketch, "E32.trimOffspring", {"start": v(25.03, -1.54) * mm, "mid": v(25.06, -0.79) * mm, "end": v(25.07, -0.03) * mm});
            skArc(sketch, "E33.trimOffspring", {"start": v(24.66, -4.55) * mm, "mid": v(24.79, -3.8) * mm, "end": v(24.9, -3.05) * mm});
            skArc(sketch, "E34.trimOffspring", {"start": v(23.94, -7.49) * mm, "mid": v(24.15, -6.76) * mm, "end": v(24.35, -6.03) * mm});
            skArc(sketch, "E35.trimOffspring", {"start": v(22.86, -10.32) * mm, "mid": v(23.17, -9.62) * mm, "end": v(23.44, -8.92) * mm});
            skArc(sketch, "E36.trimOffspring", {"start": v(21.46, -13) * mm, "mid": v(21.84, -12.35) * mm, "end": v(22.2, -11.68) * mm});
            skArc(sketch, "E37.trimOffspring", {"start": v(19.74, -15.5) * mm, "mid": v(20.2, -14.89) * mm, "end": v(20.64, -14.27) * mm});
            skArc(sketch, "E38.trimOffspring", {"start": v(17.73, -17.76) * mm, "mid": v(18.26, -17.22) * mm, "end": v(18.77, -16.66) * mm});
            skArc(sketch, "E39.trimOffspring", {"start": v(15.46, -19.77) * mm, "mid": v(16.05, -19.3) * mm, "end": v(16.63, -18.8) * mm});
            skArc(sketch, "E40.trimOffspring", {"start": v(12.97, -21.49) * mm, "mid": v(13.61, -21.09) * mm, "end": v(14.24, -20.66) * mm});
            skArc(sketch, "E41.trimOffspring", {"start": v(10.3, -22.9) * mm, "mid": v(10.98, -22.57) * mm, "end": v(11.65, -22.23) * mm});
            skArc(sketch, "E42.trimOffspring", {"start": v(7.46, -23.97) * mm, "mid": v(8.18, -23.73) * mm, "end": v(8.9, -23.47) * mm});
            skArc(sketch, "E43.trimOffspring", {"start": v(4.52, -24.7) * mm, "mid": v(5.26, -24.54) * mm, "end": v(6, -24.37) * mm});
            skArc(sketch, "E44.trimOffspring", {"start": v(1.51, -25.06) * mm, "mid": v(2.27, -25) * mm, "end": v(3.02, -24.92) * mm});
            skArc(sketch, "E45.trimOffspring", {"start": v(-1.51, -25.06) * mm, "mid": v(-0.76, -25.1) * mm, "end": v(0, -25.1) * mm});
            skArc(sketch, "E46.trimOffspring", {"start": v(-4.52, -24.7) * mm, "mid": v(-3.77, -24.82) * mm, "end": v(-3.02, -24.92) * mm});
            skArc(sketch, "E47.trimOffspring", {"start": v(-7.46, -23.97) * mm, "mid": v(-6.73, -24.18) * mm, "end": v(-6, -24.37) * mm});
            skArc(sketch, "E48.trimOffspring", {"start": v(-10.3, -22.9) * mm, "mid": v(-9.6, -23.2) * mm, "end": v(-8.9, -23.47) * mm});
            skArc(sketch, "E49.trimOffspring", {"start": v(-12.97, -21.49) * mm, "mid": v(-12.32, -21.87) * mm, "end": v(-11.65, -22.23) * mm});
            skArc(sketch, "E50.trimOffspring", {"start": v(-15.46, -19.77) * mm, "mid": v(-14.86, -20.22) * mm, "end": v(-14.24, -20.66) * mm});
            skArc(sketch, "E51.trimOffspring", {"start": v(-17.73, -17.76) * mm, "mid": v(-17.19, -18.29) * mm, "end": v(-16.63, -18.8) * mm});
            skArc(sketch, "E52.trimOffspring", {"start": v(-19.74, -15.5) * mm, "mid": v(-19.26, -16.08) * mm, "end": v(-18.77, -16.66) * mm});
            skArc(sketch, "E53.trimOffspring", {"start": v(-21.46, -13) * mm, "mid": v(-21.06, -13.64) * mm, "end": v(-20.64, -14.27) * mm});
            skArc(sketch, "E54.trimOffspring", {"start": v(-22.87, -10.32) * mm, "mid": v(-22.54, -11) * mm, "end": v(-22.2, -11.68) * mm});
            skLineSegment(sketch, "E55", {"start": v(-21.46, 12.94) * mm, "end": v(-22.2, 11.62) * mm});
            skLineSegment(sketch, "E56", {"start": v(-22.86, 10.26) * mm, "end": v(-23.44, 8.86) * mm});
            skLineSegment(sketch, "E57", {"start": v(-23.94, 7.43) * mm, "end": v(-24.35, 5.97) * mm});
            skLineSegment(sketch, "E58", {"start": v(-24.66, 4.5) * mm, "end": v(-24.9, 3) * mm});
            skLineSegment(sketch, "E59", {"start": v(-16.63, 18.74) * mm, "end": v(-15.46, 19.71) * mm});
            skSolve(sketch);
        }
        {
            var Q0;
            Q0=makeQuery(id+"F0.imprint","IMPRINT",FACE,{"disambiguationData":[TD([[makeQuery(id+"F0.imprint","IMPRINT",EDGE,{"derivedFrom":sQuery(id+"F0.wireOp",EDGE,"E0")}),-1.0]])]});
            extrude(context, id + "F1", {"entities" : qUnion([Q0]), "depth" : 10 * mm});
        }
        {
            var Q0;
            Q0=makeQuery(id+"F1.opExtrude","SWEPT_EDGE",EDGE,{"disambiguationData":[OSD([sQuery(id+"F0.wireOp",EDGE,"E6.6.1"),sQuery(id+"F0.wireOp",EDGE,"E59")])]});
            var Q1;
            Q1=makeQuery(id+"F1.opExtrude","SWEPT_EDGE",EDGE,{"disambiguationData":[OSD([sQuery(id+"F0.wireOp",EDGE,"E6.5.0"),sQuery(id+"F0.wireOp",EDGE,"E59")])]});
            var Q2;
            Q2=makeQuery(id+"F1.opExtrude","SWEPT_EDGE",EDGE,{"disambiguationData":[OSD([sQuery(id+"F0.wireOp",EDGE,"E6.6.0"),sQuery(id+"F0.wireOp",EDGE,"E24.trimOffspring")])]});
            var Q3;
            Q3=makeQuery(id+"F1.opExtrude","SWEPT_EDGE",EDGE,{"disambiguationData":[OSD([sQuery(id+"F0.wireOp",EDGE,"E6.7.1"),sQuery(id+"F0.wireOp",EDGE,"E24.trimOffspring")])]});
            var Q4;
            Q4=makeQuery(id+"F1.opExtrude","SWEPT_EDGE",EDGE,{"disambiguationData":[OSD([sQuery(id+"F0.wireOp",EDGE,"E6.7.0"),sQuery(id+"F0.wireOp",EDGE,"E25.trimOffspring")])]});
            var Q5;
            Q5=makeQuery(id+"F1.opExtrude","SWEPT_EDGE",EDGE,{"disambiguationData":[OSD([sQuery(id+"F0.wireOp",EDGE,"E6.8.1"),sQuery(id+"F0.wireOp",EDGE,"E25.trimOffspring")])]});
            var Q6;
            Q6=makeQuery(id+"F1.opExtrude","SWEPT_EDGE",EDGE,{"disambiguationData":[OSD([sQuery(id+"F0.wireOp",EDGE,"E6.5.1"),sQuery(id+"F0.wireOp",EDGE,"E20.trimOffspring")])]});
            var Q7;
            Q7=makeQuery(id+"F1.opExtrude","SWEPT_EDGE",EDGE,{"disambiguationData":[OSD([sQuery(id+"F0.wireOp",EDGE,"E6.4.0"),sQuery(id+"F0.wireOp",EDGE,"E20.trimOffspring")])]});
            var Q8;
            Q8=makeQuery(id+"F1.opExtrude","SWEPT_EDGE",EDGE,{"disambiguationData":[OSD([sQuery(id+"F0.wireOp",EDGE,"E6.4.1"),sQuery(id+"F0.wireOp",EDGE,"E23.trimOffspring")])]});
            var Q9;
            Q9=makeQuery(id+"F1.opExtrude","SWEPT_EDGE",EDGE,{"disambiguationData":[OSD([sQuery(id+"F0.wireOp",EDGE,"E6.3.0"),sQuery(id+"F0.wireOp",EDGE,"E23.trimOffspring")])]});
            var Q10;
            Q10=makeQuery(id+"F1.opExtrude","SWEPT_EDGE",EDGE,{"disambiguationData":[OSD([sQuery(id+"F0.wireOp",EDGE,"E6.3.1"),sQuery(id+"F0.wireOp",EDGE,"E19.trimOffspring")])]});
            var Q11;
            Q11=makeQuery(id+"F1.opExtrude","SWEPT_EDGE",EDGE,{"disambiguationData":[OSD([sQuery(id+"F0.wireOp",EDGE,"E6.2.0"),sQuery(id+"F0.wireOp",EDGE,"E19.trimOffspring")])]});
            var Q12;
            Q12=makeQuery(id+"F1.opExtrude","SWEPT_EDGE",EDGE,{"disambiguationData":[OSD([sQuery(id+"F0.wireOp",EDGE,"E6.2.1"),sQuery(id+"F0.wireOp",EDGE,"E21")])]});
            var Q13;
            Q13=makeQuery(id+"F1.opExtrude","SWEPT_EDGE",EDGE,{"disambiguationData":[OSD([sQuery(id+"F0.wireOp",EDGE,"E6.1.0"),sQuery(id+"F0.wireOp",EDGE,"E21")])]});
            var Q14;
            Q14=makeQuery(id+"F1.opExtrude","SWEPT_EDGE",EDGE,{"disambiguationData":[OSD([sQuery(id+"F0.wireOp",EDGE,"E6.1.1"),sQuery(id+"F0.wireOp",EDGE,"E22")])]});
            var Q15;
            Q15=makeQuery(id+"F1.opExtrude","SWEPT_EDGE",EDGE,{"disambiguationData":[OSD([sQuery(id+"F0.wireOp",EDGE,"E3.0.MirrorCS"),sQuery(id+"F0.wireOp",EDGE,"E22")])]});
            var Q16;
            Q16=makeQuery(id+"F1.opExtrude","SWEPT_EDGE",EDGE,{"disambiguationData":[OSD([sQuery(id+"F0.wireOp",EDGE,"E0"),sQuery(id+"F0.wireOp",EDGE,"E8.trimOffspring")])]});
            var Q17;
            Q17=makeQuery(id+"F1.opExtrude","SWEPT_EDGE",EDGE,{"disambiguationData":[OSD([sQuery(id+"F0.wireOp",EDGE,"E6.51.0"),sQuery(id+"F0.wireOp",EDGE,"E8.trimOffspring")])]});
            var Q18;
            Q18=makeQuery(id+"F1.opExtrude","SWEPT_EDGE",EDGE,{"disambiguationData":[OSD([sQuery(id+"F0.wireOp",EDGE,"E6.51.1"),sQuery(id+"F0.wireOp",EDGE,"E9.trimOffspring")])]});
            var Q19;
            Q19=makeQuery(id+"F1.opExtrude","SWEPT_EDGE",EDGE,{"disambiguationData":[OSD([sQuery(id+"F0.wireOp",EDGE,"E6.50.0"),sQuery(id+"F0.wireOp",EDGE,"E9.trimOffspring")])]});
            var Q20;
            Q20=makeQuery(id+"F1.opExtrude","SWEPT_EDGE",EDGE,{"disambiguationData":[OSD([sQuery(id+"F0.wireOp",EDGE,"E6.50.1"),sQuery(id+"F0.wireOp",EDGE,"E10.trimOffspring")])]});
            var Q21;
            Q21=makeQuery(id+"F1.opExtrude","SWEPT_EDGE",EDGE,{"disambiguationData":[OSD([sQuery(id+"F0.wireOp",EDGE,"E6.49.0"),sQuery(id+"F0.wireOp",EDGE,"E10.trimOffspring")])]});
            var Q22;
            Q22=makeQuery(id+"F1.opExtrude","SWEPT_EDGE",EDGE,{"disambiguationData":[OSD([sQuery(id+"F0.wireOp",EDGE,"E6.8.0"),sQuery(id+"F0.wireOp",EDGE,"E55")])]});
            var Q23;
            Q23=makeQuery(id+"F1.opExtrude","SWEPT_EDGE",EDGE,{"disambiguationData":[OSD([sQuery(id+"F0.wireOp",EDGE,"E6.9.1"),sQuery(id+"F0.wireOp",EDGE,"E55")])]});
            var Q24;
            Q24=makeQuery(id+"F1.opExtrude","SWEPT_EDGE",EDGE,{"disambiguationData":[OSD([sQuery(id+"F0.wireOp",EDGE,"E6.9.0"),sQuery(id+"F0.wireOp",EDGE,"E56")])]});
            var Q25;
            Q25=makeQuery(id+"F1.opExtrude","SWEPT_EDGE",EDGE,{"disambiguationData":[OSD([sQuery(id+"F0.wireOp",EDGE,"E6.10.1"),sQuery(id+"F0.wireOp",EDGE,"E56")])]});
            var Q26;
            Q26=makeQuery(id+"F1.opExtrude","SWEPT_EDGE",EDGE,{"disambiguationData":[OSD([sQuery(id+"F0.wireOp",EDGE,"E6.10.0"),sQuery(id+"F0.wireOp",EDGE,"E57")])]});
            var Q27;
            Q27=makeQuery(id+"F1.opExtrude","SWEPT_EDGE",EDGE,{"disambiguationData":[OSD([sQuery(id+"F0.wireOp",EDGE,"E6.11.1"),sQuery(id+"F0.wireOp",EDGE,"E57")])]});
            var Q28;
            Q28=makeQuery(id+"F1.opExtrude","SWEPT_EDGE",EDGE,{"disambiguationData":[OSD([sQuery(id+"F0.wireOp",EDGE,"E6.11.0"),sQuery(id+"F0.wireOp",EDGE,"E58")])]});
            var Q29;
            Q29=makeQuery(id+"F1.opExtrude","SWEPT_EDGE",EDGE,{"disambiguationData":[OSD([sQuery(id+"F0.wireOp",EDGE,"E6.12.1"),sQuery(id+"F0.wireOp",EDGE,"E58")])]});
            var Q30;
            Q30=makeQuery(id+"F1.opExtrude","SWEPT_EDGE",EDGE,{"disambiguationData":[OSD([sQuery(id+"F0.wireOp",EDGE,"E6.12.0"),sQuery(id+"F0.wireOp",EDGE,"E26.trimOffspring")])]});
            var Q31;
            Q31=makeQuery(id+"F1.opExtrude","SWEPT_EDGE",EDGE,{"disambiguationData":[OSD([sQuery(id+"F0.wireOp",EDGE,"E6.13.1"),sQuery(id+"F0.wireOp",EDGE,"E26.trimOffspring")])]});
            var Q32;
            Q32=makeQuery(id+"F1.opExtrude","SWEPT_EDGE",EDGE,{"disambiguationData":[OSD([sQuery(id+"F0.wireOp",EDGE,"E6.13.0"),sQuery(id+"F0.wireOp",EDGE,"E27.trimOffspring")])]});
            var Q33;
            Q33=makeQuery(id+"F1.opExtrude","SWEPT_EDGE",EDGE,{"disambiguationData":[OSD([sQuery(id+"F0.wireOp",EDGE,"E6.14.1"),sQuery(id+"F0.wireOp",EDGE,"E27.trimOffspring")])]});
            var Q34;
            Q34=makeQuery(id+"F1.opExtrude","SWEPT_EDGE",EDGE,{"disambiguationData":[OSD([sQuery(id+"F0.wireOp",EDGE,"E6.14.0"),sQuery(id+"F0.wireOp",EDGE,"E28.trimOffspring")])]});
            var Q35;
            Q35=makeQuery(id+"F1.opExtrude","SWEPT_EDGE",EDGE,{"disambiguationData":[OSD([sQuery(id+"F0.wireOp",EDGE,"E6.15.1"),sQuery(id+"F0.wireOp",EDGE,"E28.trimOffspring")])]});
            var Q36;
            Q36=makeQuery(id+"F1.opExtrude","SWEPT_EDGE",EDGE,{"disambiguationData":[OSD([sQuery(id+"F0.wireOp",EDGE,"E6.15.0"),sQuery(id+"F0.wireOp",EDGE,"E29.trimOffspring")])]});
            var Q37;
            Q37=makeQuery(id+"F1.opExtrude","SWEPT_EDGE",EDGE,{"disambiguationData":[OSD([sQuery(id+"F0.wireOp",EDGE,"E6.16.1"),sQuery(id+"F0.wireOp",EDGE,"E29.trimOffspring")])]});
            var Q38;
            Q38=makeQuery(id+"F1.opExtrude","SWEPT_EDGE",EDGE,{"disambiguationData":[OSD([sQuery(id+"F0.wireOp",EDGE,"E6.16.0"),sQuery(id+"F0.wireOp",EDGE,"E54.trimOffspring")])]});
            var Q39;
            Q39=makeQuery(id+"F1.opExtrude","SWEPT_EDGE",EDGE,{"disambiguationData":[OSD([sQuery(id+"F0.wireOp",EDGE,"E6.17.1"),sQuery(id+"F0.wireOp",EDGE,"E54.trimOffspring")])]});
            var Q40;
            Q40=makeQuery(id+"F1.opExtrude","SWEPT_EDGE",EDGE,{"disambiguationData":[OSD([sQuery(id+"F0.wireOp",EDGE,"E6.17.0"),sQuery(id+"F0.wireOp",EDGE,"E53.trimOffspring")])]});
            var Q41;
            Q41=makeQuery(id+"F1.opExtrude","SWEPT_EDGE",EDGE,{"disambiguationData":[OSD([sQuery(id+"F0.wireOp",EDGE,"E6.49.1"),sQuery(id+"F0.wireOp",EDGE,"E11.trimOffspring")])]});
            var Q42;
            Q42=makeQuery(id+"F1.opExtrude","SWEPT_EDGE",EDGE,{"disambiguationData":[OSD([sQuery(id+"F0.wireOp",EDGE,"E6.48.0"),sQuery(id+"F0.wireOp",EDGE,"E11.trimOffspring")])]});
            var Q43;
            Q43=makeQuery(id+"F1.opExtrude","SWEPT_EDGE",EDGE,{"disambiguationData":[OSD([sQuery(id+"F0.wireOp",EDGE,"E6.48.1"),sQuery(id+"F0.wireOp",EDGE,"E12.trimOffspring")])]});
            var Q44;
            Q44=makeQuery(id+"F1.opExtrude","SWEPT_EDGE",EDGE,{"disambiguationData":[OSD([sQuery(id+"F0.wireOp",EDGE,"E6.47.0"),sQuery(id+"F0.wireOp",EDGE,"E12.trimOffspring")])]});
            var Q45;
            Q45=makeQuery(id+"F1.opExtrude","SWEPT_EDGE",EDGE,{"disambiguationData":[OSD([sQuery(id+"F0.wireOp",EDGE,"E6.47.1"),sQuery(id+"F0.wireOp",EDGE,"E13.trimOffspring")])]});
            var Q46;
            Q46=makeQuery(id+"F1.opExtrude","SWEPT_EDGE",EDGE,{"disambiguationData":[OSD([sQuery(id+"F0.wireOp",EDGE,"E6.46.0"),sQuery(id+"F0.wireOp",EDGE,"E13.trimOffspring")])]});
            var Q47;
            Q47=makeQuery(id+"F1.opExtrude","SWEPT_EDGE",EDGE,{"disambiguationData":[OSD([sQuery(id+"F0.wireOp",EDGE,"E6.46.1"),sQuery(id+"F0.wireOp",EDGE,"E14.trimOffspring")])]});
            var Q48;
            Q48=makeQuery(id+"F1.opExtrude","SWEPT_EDGE",EDGE,{"disambiguationData":[OSD([sQuery(id+"F0.wireOp",EDGE,"E6.45.0"),sQuery(id+"F0.wireOp",EDGE,"E14.trimOffspring")])]});
            var Q49;
            Q49=makeQuery(id+"F1.opExtrude","SWEPT_EDGE",EDGE,{"disambiguationData":[OSD([sQuery(id+"F0.wireOp",EDGE,"E6.45.1"),sQuery(id+"F0.wireOp",EDGE,"E15.trimOffspring")])]});
            var Q50;
            Q50=makeQuery(id+"F1.opExtrude","SWEPT_EDGE",EDGE,{"disambiguationData":[OSD([sQuery(id+"F0.wireOp",EDGE,"E6.44.0"),sQuery(id+"F0.wireOp",EDGE,"E15.trimOffspring")])]});
            var Q51;
            Q51=makeQuery(id+"F1.opExtrude","SWEPT_EDGE",EDGE,{"disambiguationData":[OSD([sQuery(id+"F0.wireOp",EDGE,"E6.44.1"),sQuery(id+"F0.wireOp",EDGE,"E16.trimOffspring")])]});
            var Q52;
            Q52=makeQuery(id+"F1.opExtrude","SWEPT_EDGE",EDGE,{"disambiguationData":[OSD([sQuery(id+"F0.wireOp",EDGE,"E6.43.0"),sQuery(id+"F0.wireOp",EDGE,"E16.trimOffspring")])]});
            var Q53;
            Q53=makeQuery(id+"F1.opExtrude","SWEPT_EDGE",EDGE,{"disambiguationData":[OSD([sQuery(id+"F0.wireOp",EDGE,"E6.43.1"),sQuery(id+"F0.wireOp",EDGE,"E17.trimOffspring")])]});
            var Q54;
            Q54=makeQuery(id+"F1.opExtrude","SWEPT_EDGE",EDGE,{"disambiguationData":[OSD([sQuery(id+"F0.wireOp",EDGE,"E6.42.0"),sQuery(id+"F0.wireOp",EDGE,"E17.trimOffspring")])]});
            var Q55;
            Q55=makeQuery(id+"F1.opExtrude","SWEPT_EDGE",EDGE,{"disambiguationData":[OSD([sQuery(id+"F0.wireOp",EDGE,"E6.42.1"),sQuery(id+"F0.wireOp",EDGE,"E18.trimOffspring")])]});
            var Q56;
            Q56=makeQuery(id+"F1.opExtrude","SWEPT_EDGE",EDGE,{"disambiguationData":[OSD([sQuery(id+"F0.wireOp",EDGE,"E6.41.0"),sQuery(id+"F0.wireOp",EDGE,"E18.trimOffspring")])]});
            var Q57;
            Q57=makeQuery(id+"F1.opExtrude","SWEPT_EDGE",EDGE,{"disambiguationData":[OSD([sQuery(id+"F0.wireOp",EDGE,"E6.41.1"),sQuery(id+"F0.wireOp",EDGE,"E30.trimOffspring")])]});
            var Q58;
            Q58=makeQuery(id+"F1.opExtrude","SWEPT_EDGE",EDGE,{"disambiguationData":[OSD([sQuery(id+"F0.wireOp",EDGE,"E6.40.0"),sQuery(id+"F0.wireOp",EDGE,"E30.trimOffspring")])]});
            var Q59;
            Q59=makeQuery(id+"F1.opExtrude","SWEPT_EDGE",EDGE,{"disambiguationData":[OSD([sQuery(id+"F0.wireOp",EDGE,"E6.40.1"),sQuery(id+"F0.wireOp",EDGE,"E31.trimOffspring")])]});
            var Q60;
            Q60=makeQuery(id+"F1.opExtrude","SWEPT_EDGE",EDGE,{"disambiguationData":[OSD([sQuery(id+"F0.wireOp",EDGE,"E6.39.0"),sQuery(id+"F0.wireOp",EDGE,"E31.trimOffspring")])]});
            var Q61;
            Q61=makeQuery(id+"F1.opExtrude","SWEPT_EDGE",EDGE,{"disambiguationData":[OSD([sQuery(id+"F0.wireOp",EDGE,"E6.39.1"),sQuery(id+"F0.wireOp",EDGE,"E32.trimOffspring")])]});
            var Q62;
            Q62=makeQuery(id+"F1.opExtrude","SWEPT_EDGE",EDGE,{"disambiguationData":[OSD([sQuery(id+"F0.wireOp",EDGE,"E6.38.0"),sQuery(id+"F0.wireOp",EDGE,"E32.trimOffspring")])]});
            var Q63;
            Q63=makeQuery(id+"F1.opExtrude","SWEPT_EDGE",EDGE,{"disambiguationData":[OSD([sQuery(id+"F0.wireOp",EDGE,"E6.38.1"),sQuery(id+"F0.wireOp",EDGE,"E33.trimOffspring")])]});
            var Q64;
            Q64=makeQuery(id+"F1.opExtrude","SWEPT_EDGE",EDGE,{"disambiguationData":[OSD([sQuery(id+"F0.wireOp",EDGE,"E6.37.0"),sQuery(id+"F0.wireOp",EDGE,"E33.trimOffspring")])]});
            var Q65;
            Q65=makeQuery(id+"F1.opExtrude","SWEPT_EDGE",EDGE,{"disambiguationData":[OSD([sQuery(id+"F0.wireOp",EDGE,"E6.37.1"),sQuery(id+"F0.wireOp",EDGE,"E34.trimOffspring")])]});
            var Q66;
            Q66=makeQuery(id+"F1.opExtrude","SWEPT_EDGE",EDGE,{"disambiguationData":[OSD([sQuery(id+"F0.wireOp",EDGE,"E6.36.0"),sQuery(id+"F0.wireOp",EDGE,"E34.trimOffspring")])]});
            var Q67;
            Q67=makeQuery(id+"F1.opExtrude","SWEPT_EDGE",EDGE,{"disambiguationData":[OSD([sQuery(id+"F0.wireOp",EDGE,"E6.36.1"),sQuery(id+"F0.wireOp",EDGE,"E35.trimOffspring")])]});
            var Q68;
            Q68=makeQuery(id+"F1.opExtrude","SWEPT_EDGE",EDGE,{"disambiguationData":[OSD([sQuery(id+"F0.wireOp",EDGE,"E6.35.0"),sQuery(id+"F0.wireOp",EDGE,"E35.trimOffspring")])]});
            var Q69;
            Q69=makeQuery(id+"F1.opExtrude","SWEPT_EDGE",EDGE,{"disambiguationData":[OSD([sQuery(id+"F0.wireOp",EDGE,"E6.35.1"),sQuery(id+"F0.wireOp",EDGE,"E36.trimOffspring")])]});
            var Q70;
            Q70=makeQuery(id+"F1.opExtrude","SWEPT_EDGE",EDGE,{"disambiguationData":[OSD([sQuery(id+"F0.wireOp",EDGE,"E6.34.0"),sQuery(id+"F0.wireOp",EDGE,"E36.trimOffspring")])]});
            var Q71;
            Q71=makeQuery(id+"F1.opExtrude","SWEPT_EDGE",EDGE,{"disambiguationData":[OSD([sQuery(id+"F0.wireOp",EDGE,"E6.34.1"),sQuery(id+"F0.wireOp",EDGE,"E37.trimOffspring")])]});
            var Q72;
            Q72=makeQuery(id+"F1.opExtrude","SWEPT_EDGE",EDGE,{"disambiguationData":[OSD([sQuery(id+"F0.wireOp",EDGE,"E6.33.0"),sQuery(id+"F0.wireOp",EDGE,"E37.trimOffspring")])]});
            var Q73;
            Q73=makeQuery(id+"F1.opExtrude","SWEPT_EDGE",EDGE,{"disambiguationData":[OSD([sQuery(id+"F0.wireOp",EDGE,"E6.33.1"),sQuery(id+"F0.wireOp",EDGE,"E38.trimOffspring")])]});
            var Q74;
            Q74=makeQuery(id+"F1.opExtrude","SWEPT_EDGE",EDGE,{"disambiguationData":[OSD([sQuery(id+"F0.wireOp",EDGE,"E6.32.0"),sQuery(id+"F0.wireOp",EDGE,"E38.trimOffspring")])]});
            var Q75;
            Q75=makeQuery(id+"F1.opExtrude","SWEPT_EDGE",EDGE,{"disambiguationData":[OSD([sQuery(id+"F0.wireOp",EDGE,"E6.32.1"),sQuery(id+"F0.wireOp",EDGE,"E39.trimOffspring")])]});
            var Q76;
            Q76=makeQuery(id+"F1.opExtrude","SWEPT_EDGE",EDGE,{"disambiguationData":[OSD([sQuery(id+"F0.wireOp",EDGE,"E6.31.0"),sQuery(id+"F0.wireOp",EDGE,"E39.trimOffspring")])]});
            var Q77;
            Q77=makeQuery(id+"F1.opExtrude","SWEPT_EDGE",EDGE,{"disambiguationData":[OSD([sQuery(id+"F0.wireOp",EDGE,"E6.31.1"),sQuery(id+"F0.wireOp",EDGE,"E40.trimOffspring")])]});
            var Q78;
            Q78=makeQuery(id+"F1.opExtrude","SWEPT_EDGE",EDGE,{"disambiguationData":[OSD([sQuery(id+"F0.wireOp",EDGE,"E6.30.0"),sQuery(id+"F0.wireOp",EDGE,"E40.trimOffspring")])]});
            var Q79;
            Q79=makeQuery(id+"F1.opExtrude","SWEPT_EDGE",EDGE,{"disambiguationData":[OSD([sQuery(id+"F0.wireOp",EDGE,"E6.30.1"),sQuery(id+"F0.wireOp",EDGE,"E41.trimOffspring")])]});
            var Q80;
            Q80=makeQuery(id+"F1.opExtrude","SWEPT_EDGE",EDGE,{"disambiguationData":[OSD([sQuery(id+"F0.wireOp",EDGE,"E6.29.0"),sQuery(id+"F0.wireOp",EDGE,"E41.trimOffspring")])]});
            var Q81;
            Q81=makeQuery(id+"F1.opExtrude","SWEPT_EDGE",EDGE,{"disambiguationData":[OSD([sQuery(id+"F0.wireOp",EDGE,"E6.29.1"),sQuery(id+"F0.wireOp",EDGE,"E42.trimOffspring")])]});
            var Q82;
            Q82=makeQuery(id+"F1.opExtrude","SWEPT_EDGE",EDGE,{"disambiguationData":[OSD([sQuery(id+"F0.wireOp",EDGE,"E6.28.0"),sQuery(id+"F0.wireOp",EDGE,"E42.trimOffspring")])]});
            var Q83;
            Q83=makeQuery(id+"F1.opExtrude","SWEPT_EDGE",EDGE,{"disambiguationData":[OSD([sQuery(id+"F0.wireOp",EDGE,"E6.28.1"),sQuery(id+"F0.wireOp",EDGE,"E43.trimOffspring")])]});
            var Q84;
            Q84=makeQuery(id+"F1.opExtrude","SWEPT_EDGE",EDGE,{"disambiguationData":[OSD([sQuery(id+"F0.wireOp",EDGE,"E6.27.0"),sQuery(id+"F0.wireOp",EDGE,"E43.trimOffspring")])]});
            var Q85;
            Q85=makeQuery(id+"F1.opExtrude","SWEPT_EDGE",EDGE,{"disambiguationData":[OSD([sQuery(id+"F0.wireOp",EDGE,"E6.27.1"),sQuery(id+"F0.wireOp",EDGE,"E44.trimOffspring")])]});
            var Q86;
            Q86=makeQuery(id+"F1.opExtrude","SWEPT_EDGE",EDGE,{"disambiguationData":[OSD([sQuery(id+"F0.wireOp",EDGE,"E6.26.0"),sQuery(id+"F0.wireOp",EDGE,"E44.trimOffspring")])]});
            var Q87;
            Q87=makeQuery(id+"F1.opExtrude","SWEPT_EDGE",EDGE,{"disambiguationData":[OSD([sQuery(id+"F0.wireOp",EDGE,"E6.26.1"),sQuery(id+"F0.wireOp",EDGE,"E45.trimOffspring")])]});
            var Q88;
            Q88=makeQuery(id+"F1.opExtrude","SWEPT_EDGE",EDGE,{"disambiguationData":[OSD([sQuery(id+"F0.wireOp",EDGE,"E6.25.0"),sQuery(id+"F0.wireOp",EDGE,"E45.trimOffspring")])]});
            var Q89;
            Q89=makeQuery(id+"F1.opExtrude","SWEPT_EDGE",EDGE,{"disambiguationData":[OSD([sQuery(id+"F0.wireOp",EDGE,"E6.25.1"),sQuery(id+"F0.wireOp",EDGE,"E46.trimOffspring")])]});
            var Q90;
            Q90=makeQuery(id+"F1.opExtrude","SWEPT_EDGE",EDGE,{"disambiguationData":[OSD([sQuery(id+"F0.wireOp",EDGE,"E6.24.0"),sQuery(id+"F0.wireOp",EDGE,"E46.trimOffspring")])]});
            var Q91;
            Q91=makeQuery(id+"F1.opExtrude","SWEPT_EDGE",EDGE,{"disambiguationData":[OSD([sQuery(id+"F0.wireOp",EDGE,"E6.24.1"),sQuery(id+"F0.wireOp",EDGE,"E47.trimOffspring")])]});
            var Q92;
            Q92=makeQuery(id+"F1.opExtrude","SWEPT_EDGE",EDGE,{"disambiguationData":[OSD([sQuery(id+"F0.wireOp",EDGE,"E6.23.0"),sQuery(id+"F0.wireOp",EDGE,"E47.trimOffspring")])]});
            var Q93;
            Q93=makeQuery(id+"F1.opExtrude","SWEPT_EDGE",EDGE,{"disambiguationData":[OSD([sQuery(id+"F0.wireOp",EDGE,"E6.23.1"),sQuery(id+"F0.wireOp",EDGE,"E48.trimOffspring")])]});
            var Q94;
            Q94=makeQuery(id+"F1.opExtrude","SWEPT_EDGE",EDGE,{"disambiguationData":[OSD([sQuery(id+"F0.wireOp",EDGE,"E6.22.0"),sQuery(id+"F0.wireOp",EDGE,"E48.trimOffspring")])]});
            var Q95;
            Q95=makeQuery(id+"F1.opExtrude","SWEPT_EDGE",EDGE,{"disambiguationData":[OSD([sQuery(id+"F0.wireOp",EDGE,"E6.22.1"),sQuery(id+"F0.wireOp",EDGE,"E49.trimOffspring")])]});
            var Q96;
            Q96=makeQuery(id+"F1.opExtrude","SWEPT_EDGE",EDGE,{"disambiguationData":[OSD([sQuery(id+"F0.wireOp",EDGE,"E6.21.0"),sQuery(id+"F0.wireOp",EDGE,"E49.trimOffspring")])]});
            var Q97;
            Q97=makeQuery(id+"F1.opExtrude","SWEPT_EDGE",EDGE,{"disambiguationData":[OSD([sQuery(id+"F0.wireOp",EDGE,"E6.21.1"),sQuery(id+"F0.wireOp",EDGE,"E50.trimOffspring")])]});
            var Q98;
            Q98=makeQuery(id+"F1.opExtrude","SWEPT_EDGE",EDGE,{"disambiguationData":[OSD([sQuery(id+"F0.wireOp",EDGE,"E6.20.0"),sQuery(id+"F0.wireOp",EDGE,"E50.trimOffspring")])]});
            var Q99;
            Q99=makeQuery(id+"F1.opExtrude","SWEPT_EDGE",EDGE,{"disambiguationData":[OSD([sQuery(id+"F0.wireOp",EDGE,"E6.20.1"),sQuery(id+"F0.wireOp",EDGE,"E51.trimOffspring")])]});
            var Q100;
            Q100=makeQuery(id+"F1.opExtrude","SWEPT_EDGE",EDGE,{"disambiguationData":[OSD([sQuery(id+"F0.wireOp",EDGE,"E6.19.0"),sQuery(id+"F0.wireOp",EDGE,"E51.trimOffspring")])]});
            var Q101;
            Q101=makeQuery(id+"F1.opExtrude","SWEPT_EDGE",EDGE,{"disambiguationData":[OSD([sQuery(id+"F0.wireOp",EDGE,"E6.19.1"),sQuery(id+"F0.wireOp",EDGE,"E52.trimOffspring")])]});
            var Q102;
            Q102=makeQuery(id+"F1.opExtrude","SWEPT_EDGE",EDGE,{"disambiguationData":[OSD([sQuery(id+"F0.wireOp",EDGE,"E6.18.0"),sQuery(id+"F0.wireOp",EDGE,"E52.trimOffspring")])]});
            var Q103;
            Q103=makeQuery(id+"F1.opExtrude","SWEPT_EDGE",EDGE,{"disambiguationData":[OSD([sQuery(id+"F0.wireOp",EDGE,"E6.18.1"),sQuery(id+"F0.wireOp",EDGE,"E53.trimOffspring")])]});
            fillet(context, id + "F2", {"entities" : qUnion([Q0, Q1, Q2, Q3, Q4, Q5, Q6, Q7, Q8, Q9, Q10, Q11, Q12, Q13, Q14, Q15, Q16, Q17, Q18, Q19, Q20, Q21, Q22, Q23, Q24, Q25, Q26, Q27, Q28, Q29, Q30, Q31, Q32, Q33, Q34, Q35, Q36, Q37, Q38, Q39, Q40, Q41, Q42, Q43, Q44, Q45, Q46, Q47, Q48, Q49, Q50, Q51, Q52, Q53, Q54, Q55, Q56, Q57, Q58, Q59, Q60, Q61, Q62, Q63, Q64, Q65, Q66, Q67, Q68, Q69, Q70, Q71, Q72, Q73, Q74, Q75, Q76, Q77, Q78, Q79, Q80, Q81, Q82, Q83, Q84, Q85, Q86, Q87, Q88, Q89, Q90, Q91, Q92, Q93, Q94, Q95, Q96, Q97, Q98, Q99, Q100, Q101, Q102, Q103]), "radius" : .3 * mm, "tangentPropagation" : true, "allowEdgeOverflow" : false});
        }
        {
            var Q0;
            Q0=makeQuery(id+"F1.opExtrude","CAP_FACE",FACE,{"disambiguationData":[OSD([sQuery(id+"F0.wireOp",EDGE,"E0"),sQuery(id+"F0.wireOp",EDGE,"E1.trimOffspring"),sQuery(id+"F0.wireOp",EDGE,"E2.0.MirrorCS"),sQuery(id+"F0.wireOp",EDGE,"E3.0.MirrorCS"),sQuery(id+"F0.wireOp",EDGE,"E5.trimOffspring"),sQuery(id+"F0.wireOp",EDGE,"E6.1.0"),sQuery(id+"F0.wireOp",EDGE,"E6.1.1"),sQuery(id+"F0.wireOp",EDGE,"E6.1.2"),sQuery(id+"F0.wireOp",EDGE,"E6.1.3"),sQuery(id+"F0.wireOp",EDGE,"E6.1.4"),sQuery(id+"F0.wireOp",EDGE,"E6.2.0"),sQuery(id+"F0.wireOp",EDGE,"E6.2.1"),sQuery(id+"F0.wireOp",EDGE,"E6.2.2"),sQuery(id+"F0.wireOp",EDGE,"E6.2.3"),sQuery(id+"F0.wireOp",EDGE,"E6.2.4"),sQuery(id+"F0.wireOp",EDGE,"E6.3.0"),sQuery(id+"F0.wireOp",EDGE,"E6.3.1"),sQuery(id+"F0.wireOp",EDGE,"E6.3.2"),sQuery(id+"F0.wireOp",EDGE,"E6.3.3"),sQuery(id+"F0.wireOp",EDGE,"E6.3.4"),sQuery(id+"F0.wireOp",EDGE,"E6.4.0"),sQuery(id+"F0.wireOp",EDGE,"E6.4.1"),sQuery(id+"F0.wireOp",EDGE,"E6.4.2"),sQuery(id+"F0.wireOp",EDGE,"E6.4.3"),sQuery(id+"F0.wireOp",EDGE,"E6.4.4"),sQuery(id+"F0.wireOp",EDGE,"E6.5.0"),sQuery(id+"F0.wireOp",EDGE,"E6.5.1"),sQuery(id+"F0.wireOp",EDGE,"E6.5.2"),sQuery(id+"F0.wireOp",EDGE,"E6.5.3"),sQuery(id+"F0.wireOp",EDGE,"E6.5.4"),sQuery(id+"F0.wireOp",EDGE,"E6.6.0"),sQuery(id+"F0.wireOp",EDGE,"E6.6.1"),sQuery(id+"F0.wireOp",EDGE,"E6.6.2"),sQuery(id+"F0.wireOp",EDGE,"E6.6.3"),sQuery(id+"F0.wireOp",EDGE,"E6.6.4"),sQuery(id+"F0.wireOp",EDGE,"E6.7.0"),sQuery(id+"F0.wireOp",EDGE,"E6.7.1"),sQuery(id+"F0.wireOp",EDGE,"E6.7.2"),sQuery(id+"F0.wireOp",EDGE,"E6.7.3"),sQuery(id+"F0.wireOp",EDGE,"E6.7.4"),sQuery(id+"F0.wireOp",EDGE,"E6.8.0"),sQuery(id+"F0.wireOp",EDGE,"E6.8.1"),sQuery(id+"F0.wireOp",EDGE,"E6.8.2"),sQuery(id+"F0.wireOp",EDGE,"E6.8.3"),sQuery(id+"F0.wireOp",EDGE,"E6.8.4"),sQuery(id+"F0.wireOp",EDGE,"E6.9.0"),sQuery(id+"F0.wireOp",EDGE,"E6.9.1"),sQuery(id+"F0.wireOp",EDGE,"E6.9.2"),sQuery(id+"F0.wireOp",EDGE,"E6.9.3"),sQuery(id+"F0.wireOp",EDGE,"E6.9.4"),sQuery(id+"F0.wireOp",EDGE,"E6.10.0"),sQuery(id+"F0.wireOp",EDGE,"E6.10.1"),sQuery(id+"F0.wireOp",EDGE,"E6.10.2"),sQuery(id+"F0.wireOp",EDGE,"E6.10.3"),sQuery(id+"F0.wireOp",EDGE,"E6.10.4"),sQuery(id+"F0.wireOp",EDGE,"E6.11.0"),sQuery(id+"F0.wireOp",EDGE,"E6.11.1"),sQuery(id+"F0.wireOp",EDGE,"E6.11.2"),sQuery(id+"F0.wireOp",EDGE,"E6.11.3"),sQuery(id+"F0.wireOp",EDGE,"E6.11.4"),sQuery(id+"F0.wireOp",EDGE,"E6.12.0"),sQuery(id+"F0.wireOp",EDGE,"E6.12.1"),sQuery(id+"F0.wireOp",EDGE,"E6.12.2"),sQuery(id+"F0.wireOp",EDGE,"E6.12.3"),sQuery(id+"F0.wireOp",EDGE,"E6.12.4"),sQuery(id+"F0.wireOp",EDGE,"E6.13.0"),sQuery(id+"F0.wireOp",EDGE,"E6.13.1"),sQuery(id+"F0.wireOp",EDGE,"E6.13.2"),sQuery(id+"F0.wireOp",EDGE,"E6.13.3"),sQuery(id+"F0.wireOp",EDGE,"E6.13.4"),sQuery(id+"F0.wireOp",EDGE,"E6.14.0"),sQuery(id+"F0.wireOp",EDGE,"E6.14.1"),sQuery(id+"F0.wireOp",EDGE,"E6.14.2"),sQuery(id+"F0.wireOp",EDGE,"E6.14.3"),sQuery(id+"F0.wireOp",EDGE,"E6.14.4"),sQuery(id+"F0.wireOp",EDGE,"E6.15.0"),sQuery(id+"F0.wireOp",EDGE,"E6.15.1"),sQuery(id+"F0.wireOp",EDGE,"E6.15.2"),sQuery(id+"F0.wireOp",EDGE,"E6.15.3"),sQuery(id+"F0.wireOp",EDGE,"E6.15.4"),sQuery(id+"F0.wireOp",EDGE,"E6.16.0"),sQuery(id+"F0.wireOp",EDGE,"E6.16.1"),sQuery(id+"F0.wireOp",EDGE,"E6.16.2"),sQuery(id+"F0.wireOp",EDGE,"E6.16.3"),sQuery(id+"F0.wireOp",EDGE,"E6.16.4"),sQuery(id+"F0.wireOp",EDGE,"E6.17.0"),sQuery(id+"F0.wireOp",EDGE,"E6.17.1"),sQuery(id+"F0.wireOp",EDGE,"E6.17.2"),sQuery(id+"F0.wireOp",EDGE,"E6.17.3"),sQuery(id+"F0.wireOp",EDGE,"E6.17.4"),sQuery(id+"F0.wireOp",EDGE,"E6.18.0"),sQuery(id+"F0.wireOp",EDGE,"E6.18.1"),sQuery(id+"F0.wireOp",EDGE,"E6.18.2"),sQuery(id+"F0.wireOp",EDGE,"E6.18.3"),sQuery(id+"F0.wireOp",EDGE,"E6.18.4"),sQuery(id+"F0.wireOp",EDGE,"E6.19.0"),sQuery(id+"F0.wireOp",EDGE,"E6.19.1"),sQuery(id+"F0.wireOp",EDGE,"E6.19.2"),sQuery(id+"F0.wireOp",EDGE,"E6.19.3"),sQuery(id+"F0.wireOp",EDGE,"E6.19.4"),sQuery(id+"F0.wireOp",EDGE,"E6.20.0"),sQuery(id+"F0.wireOp",EDGE,"E6.20.1"),sQuery(id+"F0.wireOp",EDGE,"E6.20.2"),sQuery(id+"F0.wireOp",EDGE,"E6.20.3"),sQuery(id+"F0.wireOp",EDGE,"E6.20.4"),sQuery(id+"F0.wireOp",EDGE,"E6.21.0"),sQuery(id+"F0.wireOp",EDGE,"E6.21.1"),sQuery(id+"F0.wireOp",EDGE,"E6.21.2"),sQuery(id+"F0.wireOp",EDGE,"E6.21.3"),sQuery(id+"F0.wireOp",EDGE,"E6.21.4"),sQuery(id+"F0.wireOp",EDGE,"E6.22.0"),sQuery(id+"F0.wireOp",EDGE,"E6.22.1"),sQuery(id+"F0.wireOp",EDGE,"E6.22.2"),sQuery(id+"F0.wireOp",EDGE,"E6.22.3"),sQuery(id+"F0.wireOp",EDGE,"E6.22.4"),sQuery(id+"F0.wireOp",EDGE,"E6.23.0"),sQuery(id+"F0.wireOp",EDGE,"E6.23.1"),sQuery(id+"F0.wireOp",EDGE,"E6.23.2"),sQuery(id+"F0.wireOp",EDGE,"E6.23.3"),sQuery(id+"F0.wireOp",EDGE,"E6.23.4"),sQuery(id+"F0.wireOp",EDGE,"E6.24.0"),sQuery(id+"F0.wireOp",EDGE,"E6.24.1"),sQuery(id+"F0.wireOp",EDGE,"E6.24.2"),sQuery(id+"F0.wireOp",EDGE,"E6.24.3"),sQuery(id+"F0.wireOp",EDGE,"E6.24.4"),sQuery(id+"F0.wireOp",EDGE,"E6.25.0"),sQuery(id+"F0.wireOp",EDGE,"E6.25.1"),sQuery(id+"F0.wireOp",EDGE,"E6.25.2"),sQuery(id+"F0.wireOp",EDGE,"E6.25.3"),sQuery(id+"F0.wireOp",EDGE,"E6.25.4"),sQuery(id+"F0.wireOp",EDGE,"E6.26.0"),sQuery(id+"F0.wireOp",EDGE,"E6.26.1"),sQuery(id+"F0.wireOp",EDGE,"E6.26.2"),sQuery(id+"F0.wireOp",EDGE,"E6.26.3"),sQuery(id+"F0.wireOp",EDGE,"E6.26.4"),sQuery(id+"F0.wireOp",EDGE,"E6.27.0"),sQuery(id+"F0.wireOp",EDGE,"E6.27.1"),sQuery(id+"F0.wireOp",EDGE,"E6.27.2"),sQuery(id+"F0.wireOp",EDGE,"E6.27.3"),sQuery(id+"F0.wireOp",EDGE,"E6.27.4"),sQuery(id+"F0.wireOp",EDGE,"E6.28.0"),sQuery(id+"F0.wireOp",EDGE,"E6.28.1"),sQuery(id+"F0.wireOp",EDGE,"E6.28.2"),sQuery(id+"F0.wireOp",EDGE,"E6.28.3"),sQuery(id+"F0.wireOp",EDGE,"E6.28.4"),sQuery(id+"F0.wireOp",EDGE,"E6.29.0"),sQuery(id+"F0.wireOp",EDGE,"E6.29.1"),sQuery(id+"F0.wireOp",EDGE,"E6.29.2"),sQuery(id+"F0.wireOp",EDGE,"E6.29.3"),sQuery(id+"F0.wireOp",EDGE,"E6.29.4"),sQuery(id+"F0.wireOp",EDGE,"E6.30.0"),sQuery(id+"F0.wireOp",EDGE,"E6.30.1"),sQuery(id+"F0.wireOp",EDGE,"E6.30.2"),sQuery(id+"F0.wireOp",EDGE,"E6.30.3"),sQuery(id+"F0.wireOp",EDGE,"E6.30.4"),sQuery(id+"F0.wireOp",EDGE,"E6.31.0"),sQuery(id+"F0.wireOp",EDGE,"E6.31.1"),sQuery(id+"F0.wireOp",EDGE,"E6.31.2"),sQuery(id+"F0.wireOp",EDGE,"E6.31.3"),sQuery(id+"F0.wireOp",EDGE,"E6.31.4"),sQuery(id+"F0.wireOp",EDGE,"E6.32.0"),sQuery(id+"F0.wireOp",EDGE,"E6.32.1"),sQuery(id+"F0.wireOp",EDGE,"E6.32.2"),sQuery(id+"F0.wireOp",EDGE,"E6.32.3"),sQuery(id+"F0.wireOp",EDGE,"E6.32.4"),sQuery(id+"F0.wireOp",EDGE,"E6.33.0"),sQuery(id+"F0.wireOp",EDGE,"E6.33.1"),sQuery(id+"F0.wireOp",EDGE,"E6.33.2"),sQuery(id+"F0.wireOp",EDGE,"E6.33.3"),sQuery(id+"F0.wireOp",EDGE,"E6.33.4"),sQuery(id+"F0.wireOp",EDGE,"E6.34.0"),sQuery(id+"F0.wireOp",EDGE,"E6.34.1"),sQuery(id+"F0.wireOp",EDGE,"E6.34.2"),sQuery(id+"F0.wireOp",EDGE,"E6.34.3"),sQuery(id+"F0.wireOp",EDGE,"E6.34.4"),sQuery(id+"F0.wireOp",EDGE,"E6.35.0"),sQuery(id+"F0.wireOp",EDGE,"E6.35.1"),sQuery(id+"F0.wireOp",EDGE,"E6.35.2"),sQuery(id+"F0.wireOp",EDGE,"E6.35.3"),sQuery(id+"F0.wireOp",EDGE,"E6.35.4"),sQuery(id+"F0.wireOp",EDGE,"E6.36.0"),sQuery(id+"F0.wireOp",EDGE,"E6.36.1"),sQuery(id+"F0.wireOp",EDGE,"E6.36.2"),sQuery(id+"F0.wireOp",EDGE,"E6.36.3"),sQuery(id+"F0.wireOp",EDGE,"E6.36.4"),sQuery(id+"F0.wireOp",EDGE,"E6.37.0"),sQuery(id+"F0.wireOp",EDGE,"E6.37.1"),sQuery(id+"F0.wireOp",EDGE,"E6.37.2"),sQuery(id+"F0.wireOp",EDGE,"E6.37.3"),sQuery(id+"F0.wireOp",EDGE,"E6.37.4"),sQuery(id+"F0.wireOp",EDGE,"E6.38.0"),sQuery(id+"F0.wireOp",EDGE,"E6.38.1"),sQuery(id+"F0.wireOp",EDGE,"E6.38.2"),sQuery(id+"F0.wireOp",EDGE,"E6.38.3"),sQuery(id+"F0.wireOp",EDGE,"E6.38.4"),sQuery(id+"F0.wireOp",EDGE,"E6.39.0"),sQuery(id+"F0.wireOp",EDGE,"E6.39.1"),sQuery(id+"F0.wireOp",EDGE,"E6.39.2"),sQuery(id+"F0.wireOp",EDGE,"E6.39.3"),sQuery(id+"F0.wireOp",EDGE,"E6.39.4"),sQuery(id+"F0.wireOp",EDGE,"E6.40.0"),sQuery(id+"F0.wireOp",EDGE,"E6.40.1"),sQuery(id+"F0.wireOp",EDGE,"E6.40.2"),sQuery(id+"F0.wireOp",EDGE,"E6.40.3"),sQuery(id+"F0.wireOp",EDGE,"E6.40.4"),sQuery(id+"F0.wireOp",EDGE,"E6.41.0"),sQuery(id+"F0.wireOp",EDGE,"E6.41.1"),sQuery(id+"F0.wireOp",EDGE,"E6.41.2"),sQuery(id+"F0.wireOp",EDGE,"E6.41.3"),sQuery(id+"F0.wireOp",EDGE,"E6.41.4"),sQuery(id+"F0.wireOp",EDGE,"E6.42.0"),sQuery(id+"F0.wireOp",EDGE,"E6.42.1"),sQuery(id+"F0.wireOp",EDGE,"E6.42.2"),sQuery(id+"F0.wireOp",EDGE,"E6.42.3"),sQuery(id+"F0.wireOp",EDGE,"E6.42.4"),sQuery(id+"F0.wireOp",EDGE,"E6.43.0"),sQuery(id+"F0.wireOp",EDGE,"E6.43.1"),sQuery(id+"F0.wireOp",EDGE,"E6.43.2"),sQuery(id+"F0.wireOp",EDGE,"E6.43.3"),sQuery(id+"F0.wireOp",EDGE,"E6.43.4"),sQuery(id+"F0.wireOp",EDGE,"E6.44.0"),sQuery(id+"F0.wireOp",EDGE,"E6.44.1"),sQuery(id+"F0.wireOp",EDGE,"E6.44.2"),sQuery(id+"F0.wireOp",EDGE,"E6.44.3"),sQuery(id+"F0.wireOp",EDGE,"E6.44.4"),sQuery(id+"F0.wireOp",EDGE,"E6.45.0"),sQuery(id+"F0.wireOp",EDGE,"E6.45.1"),sQuery(id+"F0.wireOp",EDGE,"E6.45.2"),sQuery(id+"F0.wireOp",EDGE,"E6.45.3"),sQuery(id+"F0.wireOp",EDGE,"E6.45.4"),sQuery(id+"F0.wireOp",EDGE,"E6.46.0"),sQuery(id+"F0.wireOp",EDGE,"E6.46.1"),sQuery(id+"F0.wireOp",EDGE,"E6.46.2"),sQuery(id+"F0.wireOp",EDGE,"E6.46.3"),sQuery(id+"F0.wireOp",EDGE,"E6.46.4"),sQuery(id+"F0.wireOp",EDGE,"E6.47.0"),sQuery(id+"F0.wireOp",EDGE,"E6.47.1"),sQuery(id+"F0.wireOp",EDGE,"E6.47.2"),sQuery(id+"F0.wireOp",EDGE,"E6.47.3"),sQuery(id+"F0.wireOp",EDGE,"E6.47.4"),sQuery(id+"F0.wireOp",EDGE,"E6.48.0"),sQuery(id+"F0.wireOp",EDGE,"E6.48.1"),sQuery(id+"F0.wireOp",EDGE,"E6.48.2"),sQuery(id+"F0.wireOp",EDGE,"E6.48.3"),sQuery(id+"F0.wireOp",EDGE,"E6.48.4"),sQuery(id+"F0.wireOp",EDGE,"E6.49.0"),sQuery(id+"F0.wireOp",EDGE,"E6.49.1"),sQuery(id+"F0.wireOp",EDGE,"E6.49.2"),sQuery(id+"F0.wireOp",EDGE,"E6.49.3"),sQuery(id+"F0.wireOp",EDGE,"E6.49.4"),sQuery(id+"F0.wireOp",EDGE,"E6.50.0"),sQuery(id+"F0.wireOp",EDGE,"E6.50.1"),sQuery(id+"F0.wireOp",EDGE,"E6.50.2"),sQuery(id+"F0.wireOp",EDGE,"E6.50.3"),sQuery(id+"F0.wireOp",EDGE,"E6.50.4"),sQuery(id+"F0.wireOp",EDGE,"E6.51.0"),sQuery(id+"F0.wireOp",EDGE,"E6.51.1"),sQuery(id+"F0.wireOp",EDGE,"E6.51.2"),sQuery(id+"F0.wireOp",EDGE,"E6.51.3"),sQuery(id+"F0.wireOp",EDGE,"E6.51.4"),sQuery(id+"F0.wireOp",EDGE,"E7"),sQuery(id+"F0.wireOp",EDGE,"E8.trimOffspring"),sQuery(id+"F0.wireOp",EDGE,"E9.trimOffspring"),sQuery(id+"F0.wireOp",EDGE,"E10.trimOffspring"),sQuery(id+"F0.wireOp",EDGE,"E11.trimOffspring"),sQuery(id+"F0.wireOp",EDGE,"E12.trimOffspring"),sQuery(id+"F0.wireOp",EDGE,"E13.trimOffspring"),sQuery(id+"F0.wireOp",EDGE,"E14.trimOffspring"),sQuery(id+"F0.wireOp",EDGE,"E15.trimOffspring"),sQuery(id+"F0.wireOp",EDGE,"E16.trimOffspring"),sQuery(id+"F0.wireOp",EDGE,"E17.trimOffspring"),sQuery(id+"F0.wireOp",EDGE,"E18.trimOffspring"),sQuery(id+"F0.wireOp",EDGE,"E19.trimOffspring"),sQuery(id+"F0.wireOp",EDGE,"E20.trimOffspring"),sQuery(id+"F0.wireOp",EDGE,"E21"),sQuery(id+"F0.wireOp",EDGE,"E22"),sQuery(id+"F0.wireOp",EDGE,"E23.trimOffspring"),sQuery(id+"F0.wireOp",EDGE,"E24.trimOffspring"),sQuery(id+"F0.wireOp",EDGE,"E25.trimOffspring"),sQuery(id+"F0.wireOp",EDGE,"E26.trimOffspring"),sQuery(id+"F0.wireOp",EDGE,"E27.trimOffspring"),sQuery(id+"F0.wireOp",EDGE,"E28.trimOffspring"),sQuery(id+"F0.wireOp",EDGE,"E29.trimOffspring"),sQuery(id+"F0.wireOp",EDGE,"E30.trimOffspring"),sQuery(id+"F0.wireOp",EDGE,"E31.trimOffspring"),sQuery(id+"F0.wireOp",EDGE,"E32.trimOffspring"),sQuery(id+"F0.wireOp",EDGE,"E33.trimOffspring"),sQuery(id+"F0.wireOp",EDGE,"E34.trimOffspring"),sQuery(id+"F0.wireOp",EDGE,"E35.trimOffspring"),sQuery(id+"F0.wireOp",EDGE,"E36.trimOffspring"),sQuery(id+"F0.wireOp",EDGE,"E37.trimOffspring"),sQuery(id+"F0.wireOp",EDGE,"E38.trimOffspring"),sQuery(id+"F0.wireOp",EDGE,"E39.trimOffspring"),sQuery(id+"F0.wireOp",EDGE,"E40.trimOffspring"),sQuery(id+"F0.wireOp",EDGE,"E41.trimOffspring"),sQuery(id+"F0.wireOp",EDGE,"E42.trimOffspring"),sQuery(id+"F0.wireOp",EDGE,"E43.trimOffspring"),sQuery(id+"F0.wireOp",EDGE,"E44.trimOffspring"),sQuery(id+"F0.wireOp",EDGE,"E45.trimOffspring"),sQuery(id+"F0.wireOp",EDGE,"E46.trimOffspring"),sQuery(id+"F0.wireOp",EDGE,"E47.trimOffspring"),sQuery(id+"F0.wireOp",EDGE,"E48.trimOffspring"),sQuery(id+"F0.wireOp",EDGE,"E49.trimOffspring"),sQuery(id+"F0.wireOp",EDGE,"E50.trimOffspring"),sQuery(id+"F0.wireOp",EDGE,"E51.trimOffspring"),sQuery(id+"F0.wireOp",EDGE,"E52.trimOffspring"),sQuery(id+"F0.wireOp",EDGE,"E53.trimOffspring"),sQuery(id+"F0.wireOp",EDGE,"E54.trimOffspring"),sQuery(id+"F0.wireOp",EDGE,"E55"),sQuery(id+"F0.wireOp",EDGE,"E56"),sQuery(id+"F0.wireOp",EDGE,"E57"),sQuery(id+"F0.wireOp",EDGE,"E58"),sQuery(id+"F0.wireOp",EDGE,"E59")])],"isStart":true});
            var sketch = newSketch(context, id + "F3", { "sketchPlane" : qUnion([Q0])});
            skCircle(sketch, "E60.0", {"center": v(0, -0.03) * mm, "radius": 29 * mm});
            skSolve(sketch);
        }
        {
            var Q0;
            {var subQ97=sQuery(id+"F0.wireOp",EDGE,"E1.trimOffspring");Q0=makeQuery(id+"F3.imprint","IMPRINT",FACE,{"disambiguationData":[TD([[makeQuery(id+"F3.imprint","IMPRINT",EDGE,{"derivedFrom":makeQuery(id+"F1.opExtrude","CAP_EDGE",EDGE,{"disambiguationData":[OSD([subQ97])],"isStart":true})}),-1.0]])]});}
            var Q1;
            Q1=makeQuery(id+"F3.imprint","IMPRINT",FACE,{"disambiguationData":[TD([[makeQuery(id+"F3.imprint","IMPRINT",EDGE,{"derivedFrom":sQuery(id+"F3.wireOp",EDGE,"E60.0")}),-1.0]])]});
            extrude(context, id + "F4", {"entities" : qUnion([Q0, Q1]), "operationType" : NewBodyOperationType.ADD, "depth" : 1 * mm});
        }
        {
            var Q0;
            Q0=makeQuery(id+"F1.opExtrude","SWEPT_BODY",BODY,{"disambiguationData":[OSD([sQuery(id+"F0.wireOp",EDGE,"E0"),sQuery(id+"F0.wireOp",EDGE,"E1.trimOffspring"),sQuery(id+"F0.wireOp",EDGE,"E2.0.MirrorCS"),sQuery(id+"F0.wireOp",EDGE,"E3.0.MirrorCS"),sQuery(id+"F0.wireOp",EDGE,"E5.trimOffspring"),sQuery(id+"F0.wireOp",EDGE,"E6.1.0"),sQuery(id+"F0.wireOp",EDGE,"E6.1.1"),sQuery(id+"F0.wireOp",EDGE,"E6.1.2"),sQuery(id+"F0.wireOp",EDGE,"E6.1.3"),sQuery(id+"F0.wireOp",EDGE,"E6.1.4"),sQuery(id+"F0.wireOp",EDGE,"E6.2.0"),sQuery(id+"F0.wireOp",EDGE,"E6.2.1"),sQuery(id+"F0.wireOp",EDGE,"E6.2.2"),sQuery(id+"F0.wireOp",EDGE,"E6.2.3"),sQuery(id+"F0.wireOp",EDGE,"E6.2.4"),sQuery(id+"F0.wireOp",EDGE,"E6.3.0"),sQuery(id+"F0.wireOp",EDGE,"E6.3.1"),sQuery(id+"F0.wireOp",EDGE,"E6.3.2"),sQuery(id+"F0.wireOp",EDGE,"E6.3.3"),sQuery(id+"F0.wireOp",EDGE,"E6.3.4"),sQuery(id+"F0.wireOp",EDGE,"E6.4.0"),sQuery(id+"F0.wireOp",EDGE,"E6.4.1"),sQuery(id+"F0.wireOp",EDGE,"E6.4.2"),sQuery(id+"F0.wireOp",EDGE,"E6.4.3"),sQuery(id+"F0.wireOp",EDGE,"E6.4.4"),sQuery(id+"F0.wireOp",EDGE,"E6.5.0"),sQuery(id+"F0.wireOp",EDGE,"E6.5.1"),sQuery(id+"F0.wireOp",EDGE,"E6.5.2"),sQuery(id+"F0.wireOp",EDGE,"E6.5.3"),sQuery(id+"F0.wireOp",EDGE,"E6.5.4"),sQuery(id+"F0.wireOp",EDGE,"E6.6.0"),sQuery(id+"F0.wireOp",EDGE,"E6.6.1"),sQuery(id+"F0.wireOp",EDGE,"E6.6.2"),sQuery(id+"F0.wireOp",EDGE,"E6.6.3"),sQuery(id+"F0.wireOp",EDGE,"E6.6.4"),sQuery(id+"F0.wireOp",EDGE,"E6.7.0"),sQuery(id+"F0.wireOp",EDGE,"E6.7.1"),sQuery(id+"F0.wireOp",EDGE,"E6.7.2"),sQuery(id+"F0.wireOp",EDGE,"E6.7.3"),sQuery(id+"F0.wireOp",EDGE,"E6.7.4"),sQuery(id+"F0.wireOp",EDGE,"E6.8.0"),sQuery(id+"F0.wireOp",EDGE,"E6.8.1"),sQuery(id+"F0.wireOp",EDGE,"E6.8.2"),sQuery(id+"F0.wireOp",EDGE,"E6.8.3"),sQuery(id+"F0.wireOp",EDGE,"E6.8.4"),sQuery(id+"F0.wireOp",EDGE,"E6.9.0"),sQuery(id+"F0.wireOp",EDGE,"E6.9.1"),sQuery(id+"F0.wireOp",EDGE,"E6.9.2"),sQuery(id+"F0.wireOp",EDGE,"E6.9.3"),sQuery(id+"F0.wireOp",EDGE,"E6.9.4"),sQuery(id+"F0.wireOp",EDGE,"E6.10.0"),sQuery(id+"F0.wireOp",EDGE,"E6.10.1"),sQuery(id+"F0.wireOp",EDGE,"E6.10.2"),sQuery(id+"F0.wireOp",EDGE,"E6.10.3"),sQuery(id+"F0.wireOp",EDGE,"E6.10.4"),sQuery(id+"F0.wireOp",EDGE,"E6.11.0"),sQuery(id+"F0.wireOp",EDGE,"E6.11.1"),sQuery(id+"F0.wireOp",EDGE,"E6.11.2"),sQuery(id+"F0.wireOp",EDGE,"E6.11.3"),sQuery(id+"F0.wireOp",EDGE,"E6.11.4"),sQuery(id+"F0.wireOp",EDGE,"E6.12.0"),sQuery(id+"F0.wireOp",EDGE,"E6.12.1"),sQuery(id+"F0.wireOp",EDGE,"E6.12.2"),sQuery(id+"F0.wireOp",EDGE,"E6.12.3"),sQuery(id+"F0.wireOp",EDGE,"E6.12.4"),sQuery(id+"F0.wireOp",EDGE,"E6.13.0"),sQuery(id+"F0.wireOp",EDGE,"E6.13.1"),sQuery(id+"F0.wireOp",EDGE,"E6.13.2"),sQuery(id+"F0.wireOp",EDGE,"E6.13.3"),sQuery(id+"F0.wireOp",EDGE,"E6.13.4"),sQuery(id+"F0.wireOp",EDGE,"E6.14.0"),sQuery(id+"F0.wireOp",EDGE,"E6.14.1"),sQuery(id+"F0.wireOp",EDGE,"E6.14.2"),sQuery(id+"F0.wireOp",EDGE,"E6.14.3"),sQuery(id+"F0.wireOp",EDGE,"E6.14.4"),sQuery(id+"F0.wireOp",EDGE,"E6.15.0"),sQuery(id+"F0.wireOp",EDGE,"E6.15.1"),sQuery(id+"F0.wireOp",EDGE,"E6.15.2"),sQuery(id+"F0.wireOp",EDGE,"E6.15.3"),sQuery(id+"F0.wireOp",EDGE,"E6.15.4"),sQuery(id+"F0.wireOp",EDGE,"E6.16.0"),sQuery(id+"F0.wireOp",EDGE,"E6.16.1"),sQuery(id+"F0.wireOp",EDGE,"E6.16.2"),sQuery(id+"F0.wireOp",EDGE,"E6.16.3"),sQuery(id+"F0.wireOp",EDGE,"E6.16.4"),sQuery(id+"F0.wireOp",EDGE,"E6.17.0"),sQuery(id+"F0.wireOp",EDGE,"E6.17.1"),sQuery(id+"F0.wireOp",EDGE,"E6.17.2"),sQuery(id+"F0.wireOp",EDGE,"E6.17.3"),sQuery(id+"F0.wireOp",EDGE,"E6.17.4"),sQuery(id+"F0.wireOp",EDGE,"E6.18.0"),sQuery(id+"F0.wireOp",EDGE,"E6.18.1"),sQuery(id+"F0.wireOp",EDGE,"E6.18.2"),sQuery(id+"F0.wireOp",EDGE,"E6.18.3"),sQuery(id+"F0.wireOp",EDGE,"E6.18.4"),sQuery(id+"F0.wireOp",EDGE,"E6.19.0"),sQuery(id+"F0.wireOp",EDGE,"E6.19.1"),sQuery(id+"F0.wireOp",EDGE,"E6.19.2"),sQuery(id+"F0.wireOp",EDGE,"E6.19.3"),sQuery(id+"F0.wireOp",EDGE,"E6.19.4"),sQuery(id+"F0.wireOp",EDGE,"E6.20.0"),sQuery(id+"F0.wireOp",EDGE,"E6.20.1"),sQuery(id+"F0.wireOp",EDGE,"E6.20.2"),sQuery(id+"F0.wireOp",EDGE,"E6.20.3"),sQuery(id+"F0.wireOp",EDGE,"E6.20.4"),sQuery(id+"F0.wireOp",EDGE,"E6.21.0"),sQuery(id+"F0.wireOp",EDGE,"E6.21.1"),sQuery(id+"F0.wireOp",EDGE,"E6.21.2"),sQuery(id+"F0.wireOp",EDGE,"E6.21.3"),sQuery(id+"F0.wireOp",EDGE,"E6.21.4"),sQuery(id+"F0.wireOp",EDGE,"E6.22.0"),sQuery(id+"F0.wireOp",EDGE,"E6.22.1"),sQuery(id+"F0.wireOp",EDGE,"E6.22.2"),sQuery(id+"F0.wireOp",EDGE,"E6.22.3"),sQuery(id+"F0.wireOp",EDGE,"E6.22.4"),sQuery(id+"F0.wireOp",EDGE,"E6.23.0"),sQuery(id+"F0.wireOp",EDGE,"E6.23.1"),sQuery(id+"F0.wireOp",EDGE,"E6.23.2"),sQuery(id+"F0.wireOp",EDGE,"E6.23.3"),sQuery(id+"F0.wireOp",EDGE,"E6.23.4"),sQuery(id+"F0.wireOp",EDGE,"E6.24.0"),sQuery(id+"F0.wireOp",EDGE,"E6.24.1"),sQuery(id+"F0.wireOp",EDGE,"E6.24.2"),sQuery(id+"F0.wireOp",EDGE,"E6.24.3"),sQuery(id+"F0.wireOp",EDGE,"E6.24.4"),sQuery(id+"F0.wireOp",EDGE,"E6.25.0"),sQuery(id+"F0.wireOp",EDGE,"E6.25.1"),sQuery(id+"F0.wireOp",EDGE,"E6.25.2"),sQuery(id+"F0.wireOp",EDGE,"E6.25.3"),sQuery(id+"F0.wireOp",EDGE,"E6.25.4"),sQuery(id+"F0.wireOp",EDGE,"E6.26.0"),sQuery(id+"F0.wireOp",EDGE,"E6.26.1"),sQuery(id+"F0.wireOp",EDGE,"E6.26.2"),sQuery(id+"F0.wireOp",EDGE,"E6.26.3"),sQuery(id+"F0.wireOp",EDGE,"E6.26.4"),sQuery(id+"F0.wireOp",EDGE,"E6.27.0"),sQuery(id+"F0.wireOp",EDGE,"E6.27.1"),sQuery(id+"F0.wireOp",EDGE,"E6.27.2"),sQuery(id+"F0.wireOp",EDGE,"E6.27.3"),sQuery(id+"F0.wireOp",EDGE,"E6.27.4"),sQuery(id+"F0.wireOp",EDGE,"E6.28.0"),sQuery(id+"F0.wireOp",EDGE,"E6.28.1"),sQuery(id+"F0.wireOp",EDGE,"E6.28.2"),sQuery(id+"F0.wireOp",EDGE,"E6.28.3"),sQuery(id+"F0.wireOp",EDGE,"E6.28.4"),sQuery(id+"F0.wireOp",EDGE,"E6.29.0"),sQuery(id+"F0.wireOp",EDGE,"E6.29.1"),sQuery(id+"F0.wireOp",EDGE,"E6.29.2"),sQuery(id+"F0.wireOp",EDGE,"E6.29.3"),sQuery(id+"F0.wireOp",EDGE,"E6.29.4"),sQuery(id+"F0.wireOp",EDGE,"E6.30.0"),sQuery(id+"F0.wireOp",EDGE,"E6.30.1"),sQuery(id+"F0.wireOp",EDGE,"E6.30.2"),sQuery(id+"F0.wireOp",EDGE,"E6.30.3"),sQuery(id+"F0.wireOp",EDGE,"E6.30.4"),sQuery(id+"F0.wireOp",EDGE,"E6.31.0"),sQuery(id+"F0.wireOp",EDGE,"E6.31.1"),sQuery(id+"F0.wireOp",EDGE,"E6.31.2"),sQuery(id+"F0.wireOp",EDGE,"E6.31.3"),sQuery(id+"F0.wireOp",EDGE,"E6.31.4"),sQuery(id+"F0.wireOp",EDGE,"E6.32.0"),sQuery(id+"F0.wireOp",EDGE,"E6.32.1"),sQuery(id+"F0.wireOp",EDGE,"E6.32.2"),sQuery(id+"F0.wireOp",EDGE,"E6.32.3"),sQuery(id+"F0.wireOp",EDGE,"E6.32.4"),sQuery(id+"F0.wireOp",EDGE,"E6.33.0"),sQuery(id+"F0.wireOp",EDGE,"E6.33.1"),sQuery(id+"F0.wireOp",EDGE,"E6.33.2"),sQuery(id+"F0.wireOp",EDGE,"E6.33.3"),sQuery(id+"F0.wireOp",EDGE,"E6.33.4"),sQuery(id+"F0.wireOp",EDGE,"E6.34.0"),sQuery(id+"F0.wireOp",EDGE,"E6.34.1"),sQuery(id+"F0.wireOp",EDGE,"E6.34.2"),sQuery(id+"F0.wireOp",EDGE,"E6.34.3"),sQuery(id+"F0.wireOp",EDGE,"E6.34.4"),sQuery(id+"F0.wireOp",EDGE,"E6.35.0"),sQuery(id+"F0.wireOp",EDGE,"E6.35.1"),sQuery(id+"F0.wireOp",EDGE,"E6.35.2"),sQuery(id+"F0.wireOp",EDGE,"E6.35.3"),sQuery(id+"F0.wireOp",EDGE,"E6.35.4"),sQuery(id+"F0.wireOp",EDGE,"E6.36.0"),sQuery(id+"F0.wireOp",EDGE,"E6.36.1"),sQuery(id+"F0.wireOp",EDGE,"E6.36.2"),sQuery(id+"F0.wireOp",EDGE,"E6.36.3"),sQuery(id+"F0.wireOp",EDGE,"E6.36.4"),sQuery(id+"F0.wireOp",EDGE,"E6.37.0"),sQuery(id+"F0.wireOp",EDGE,"E6.37.1"),sQuery(id+"F0.wireOp",EDGE,"E6.37.2"),sQuery(id+"F0.wireOp",EDGE,"E6.37.3"),sQuery(id+"F0.wireOp",EDGE,"E6.37.4"),sQuery(id+"F0.wireOp",EDGE,"E6.38.0"),sQuery(id+"F0.wireOp",EDGE,"E6.38.1"),sQuery(id+"F0.wireOp",EDGE,"E6.38.2"),sQuery(id+"F0.wireOp",EDGE,"E6.38.3"),sQuery(id+"F0.wireOp",EDGE,"E6.38.4"),sQuery(id+"F0.wireOp",EDGE,"E6.39.0"),sQuery(id+"F0.wireOp",EDGE,"E6.39.1"),sQuery(id+"F0.wireOp",EDGE,"E6.39.2"),sQuery(id+"F0.wireOp",EDGE,"E6.39.3"),sQuery(id+"F0.wireOp",EDGE,"E6.39.4"),sQuery(id+"F0.wireOp",EDGE,"E6.40.0"),sQuery(id+"F0.wireOp",EDGE,"E6.40.1"),sQuery(id+"F0.wireOp",EDGE,"E6.40.2"),sQuery(id+"F0.wireOp",EDGE,"E6.40.3"),sQuery(id+"F0.wireOp",EDGE,"E6.40.4"),sQuery(id+"F0.wireOp",EDGE,"E6.41.0"),sQuery(id+"F0.wireOp",EDGE,"E6.41.1"),sQuery(id+"F0.wireOp",EDGE,"E6.41.2"),sQuery(id+"F0.wireOp",EDGE,"E6.41.3"),sQuery(id+"F0.wireOp",EDGE,"E6.41.4"),sQuery(id+"F0.wireOp",EDGE,"E6.42.0"),sQuery(id+"F0.wireOp",EDGE,"E6.42.1"),sQuery(id+"F0.wireOp",EDGE,"E6.42.2"),sQuery(id+"F0.wireOp",EDGE,"E6.42.3"),sQuery(id+"F0.wireOp",EDGE,"E6.42.4"),sQuery(id+"F0.wireOp",EDGE,"E6.43.0"),sQuery(id+"F0.wireOp",EDGE,"E6.43.1"),sQuery(id+"F0.wireOp",EDGE,"E6.43.2"),sQuery(id+"F0.wireOp",EDGE,"E6.43.3"),sQuery(id+"F0.wireOp",EDGE,"E6.43.4"),sQuery(id+"F0.wireOp",EDGE,"E6.44.0"),sQuery(id+"F0.wireOp",EDGE,"E6.44.1"),sQuery(id+"F0.wireOp",EDGE,"E6.44.2"),sQuery(id+"F0.wireOp",EDGE,"E6.44.3"),sQuery(id+"F0.wireOp",EDGE,"E6.44.4"),sQuery(id+"F0.wireOp",EDGE,"E6.45.0"),sQuery(id+"F0.wireOp",EDGE,"E6.45.1"),sQuery(id+"F0.wireOp",EDGE,"E6.45.2"),sQuery(id+"F0.wireOp",EDGE,"E6.45.3"),sQuery(id+"F0.wireOp",EDGE,"E6.45.4"),sQuery(id+"F0.wireOp",EDGE,"E6.46.0"),sQuery(id+"F0.wireOp",EDGE,"E6.46.1"),sQuery(id+"F0.wireOp",EDGE,"E6.46.2"),sQuery(id+"F0.wireOp",EDGE,"E6.46.3"),sQuery(id+"F0.wireOp",EDGE,"E6.46.4"),sQuery(id+"F0.wireOp",EDGE,"E6.47.0"),sQuery(id+"F0.wireOp",EDGE,"E6.47.1"),sQuery(id+"F0.wireOp",EDGE,"E6.47.2"),sQuery(id+"F0.wireOp",EDGE,"E6.47.3"),sQuery(id+"F0.wireOp",EDGE,"E6.47.4"),sQuery(id+"F0.wireOp",EDGE,"E6.48.0"),sQuery(id+"F0.wireOp",EDGE,"E6.48.1"),sQuery(id+"F0.wireOp",EDGE,"E6.48.2"),sQuery(id+"F0.wireOp",EDGE,"E6.48.3"),sQuery(id+"F0.wireOp",EDGE,"E6.48.4"),sQuery(id+"F0.wireOp",EDGE,"E6.49.0"),sQuery(id+"F0.wireOp",EDGE,"E6.49.1"),sQuery(id+"F0.wireOp",EDGE,"E6.49.2"),sQuery(id+"F0.wireOp",EDGE,"E6.49.3"),sQuery(id+"F0.wireOp",EDGE,"E6.49.4"),sQuery(id+"F0.wireOp",EDGE,"E6.50.0"),sQuery(id+"F0.wireOp",EDGE,"E6.50.1"),sQuery(id+"F0.wireOp",EDGE,"E6.50.2"),sQuery(id+"F0.wireOp",EDGE,"E6.50.3"),sQuery(id+"F0.wireOp",EDGE,"E6.50.4"),sQuery(id+"F0.wireOp",EDGE,"E6.51.0"),sQuery(id+"F0.wireOp",EDGE,"E6.51.1"),sQuery(id+"F0.wireOp",EDGE,"E6.51.2"),sQuery(id+"F0.wireOp",EDGE,"E6.51.3"),sQuery(id+"F0.wireOp",EDGE,"E6.51.4"),sQuery(id+"F0.wireOp",EDGE,"E7"),sQuery(id+"F0.wireOp",EDGE,"E8.trimOffspring"),sQuery(id+"F0.wireOp",EDGE,"E9.trimOffspring"),sQuery(id+"F0.wireOp",EDGE,"E10.trimOffspring"),sQuery(id+"F0.wireOp",EDGE,"E11.trimOffspring"),sQuery(id+"F0.wireOp",EDGE,"E12.trimOffspring"),sQuery(id+"F0.wireOp",EDGE,"E13.trimOffspring"),sQuery(id+"F0.wireOp",EDGE,"E14.trimOffspring"),sQuery(id+"F0.wireOp",EDGE,"E15.trimOffspring"),sQuery(id+"F0.wireOp",EDGE,"E16.trimOffspring"),sQuery(id+"F0.wireOp",EDGE,"E17.trimOffspring"),sQuery(id+"F0.wireOp",EDGE,"E18.trimOffspring"),sQuery(id+"F0.wireOp",EDGE,"E19.trimOffspring"),sQuery(id+"F0.wireOp",EDGE,"E20.trimOffspring"),sQuery(id+"F0.wireOp",EDGE,"E21"),sQuery(id+"F0.wireOp",EDGE,"E22"),sQuery(id+"F0.wireOp",EDGE,"E23.trimOffspring"),sQuery(id+"F0.wireOp",EDGE,"E24.trimOffspring"),sQuery(id+"F0.wireOp",EDGE,"E25.trimOffspring"),sQuery(id+"F0.wireOp",EDGE,"E26.trimOffspring"),sQuery(id+"F0.wireOp",EDGE,"E27.trimOffspring"),sQuery(id+"F0.wireOp",EDGE,"E28.trimOffspring"),sQuery(id+"F0.wireOp",EDGE,"E29.trimOffspring"),sQuery(id+"F0.wireOp",EDGE,"E30.trimOffspring"),sQuery(id+"F0.wireOp",EDGE,"E31.trimOffspring"),sQuery(id+"F0.wireOp",EDGE,"E32.trimOffspring"),sQuery(id+"F0.wireOp",EDGE,"E33.trimOffspring"),sQuery(id+"F0.wireOp",EDGE,"E34.trimOffspring"),sQuery(id+"F0.wireOp",EDGE,"E35.trimOffspring"),sQuery(id+"F0.wireOp",EDGE,"E36.trimOffspring"),sQuery(id+"F0.wireOp",EDGE,"E37.trimOffspring"),sQuery(id+"F0.wireOp",EDGE,"E38.trimOffspring"),sQuery(id+"F0.wireOp",EDGE,"E39.trimOffspring"),sQuery(id+"F0.wireOp",EDGE,"E40.trimOffspring"),sQuery(id+"F0.wireOp",EDGE,"E41.trimOffspring"),sQuery(id+"F0.wireOp",EDGE,"E42.trimOffspring"),sQuery(id+"F0.wireOp",EDGE,"E43.trimOffspring"),sQuery(id+"F0.wireOp",EDGE,"E44.trimOffspring"),sQuery(id+"F0.wireOp",EDGE,"E45.trimOffspring"),sQuery(id+"F0.wireOp",EDGE,"E46.trimOffspring"),sQuery(id+"F0.wireOp",EDGE,"E47.trimOffspring"),sQuery(id+"F0.wireOp",EDGE,"E48.trimOffspring"),sQuery(id+"F0.wireOp",EDGE,"E49.trimOffspring"),sQuery(id+"F0.wireOp",EDGE,"E50.trimOffspring"),sQuery(id+"F0.wireOp",EDGE,"E51.trimOffspring"),sQuery(id+"F0.wireOp",EDGE,"E52.trimOffspring"),sQuery(id+"F0.wireOp",EDGE,"E53.trimOffspring"),sQuery(id+"F0.wireOp",EDGE,"E54.trimOffspring"),sQuery(id+"F0.wireOp",EDGE,"E55"),sQuery(id+"F0.wireOp",EDGE,"E56"),sQuery(id+"F0.wireOp",EDGE,"E57"),sQuery(id+"F0.wireOp",EDGE,"E58"),sQuery(id+"F0.wireOp",EDGE,"E59")])]});
            var Q1;
            Q1=qCreatedBy(makeId("Origin.pointOp"),VERTEX);
            transform(context, id + "F5", {"entities" : qUnion([Q0]), "transformType" : TransformType.SCALE_UNIFORMLY, "scale" : 1.02, "makeCopy" : false, "scalePoint" : qUnion([Q1])});
        }
    });
